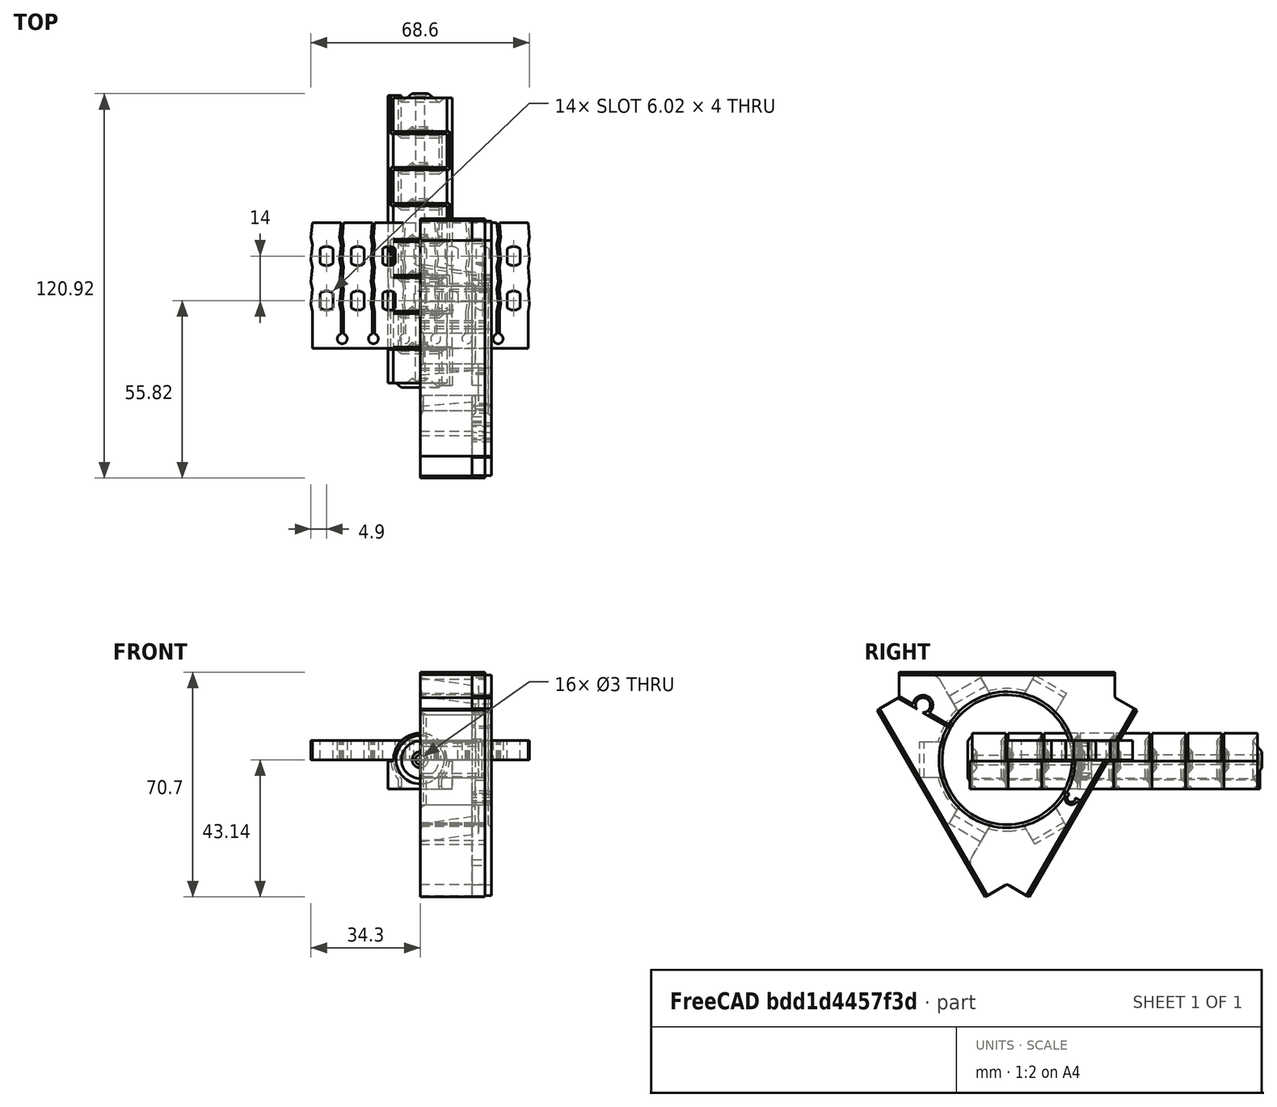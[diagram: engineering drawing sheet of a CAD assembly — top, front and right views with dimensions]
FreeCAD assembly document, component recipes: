
FREECAD ASSEMBLY — COMPONENT RECIPES ("BaseHingeModel_ver1.3_BandOnAxis")

This assembly document has 8 components, labeled P0..P7 below (a component is one placed body or linked part). 7 of them carry a construction recipe — the FreeCAD feature program that regenerates the part from scratch, quoted from this document or its linked companion documents; the rest are supplied as boundary geometry only. No exploded tour is included for this assembly.
COMPONENT P0 — geometry summary ("Assembly"; no construction recipe available for this part):
  bounding box: 182.8 x 158.8 x 20.4 mm
  tessellated surface: 20,696 triangles
  volume: 9578097130411803656351970426578674498653964242418576373807381627235447409514995756881183408189511817567906541525464308833607482709359269325981809199022080 mm^3 (1616738801575943140395693637715189882977871249383409942478852649766611869419882643060896964713126329768861879254438412431142423713072396559864123359232% of its bounding box)
COMPONENT P1 — recipe-attached ("BaseHingePart", modeled in this document).
Construction recipe (the document's own serialized feature program — sketch geometry with constraints, then the solid features built on it; lengths are millimeters unless a unit is written):

FEATURE [Sketcher::SketchObject] Sketch007  label="RightCylinderScatch"
  FullyConstrained = true
  MapMode = 5
  Support = -> [XY_Plane002]
  expr: Constraints[10] = Spreadsheet.mmDiskHight
  expr: Constraints[11] = Spreadsheet.mmLedgeStep
  expr: Constraints[12] = Spreadsheet.mmLedgeStep * 2
  expr: Constraints[13] = Spreadsheet.mmLedgeStep
  expr: Constraints[14] = Spreadsheet.mmLedgeStep / 2
  expr: Constraints[16] = Spreadsheet.mmDiskLedge
  expr: Constraints[20] = Spreadsheet.mmDiskLedge * 2
  expr: Constraints[21] = Spreadsheet.mmDiskLedge
  expr: Constraints[34] = Spreadsheet.mmAirSpace / 2
  expr: Constraints[35] = Spreadsheet.mmLedgeStep / 2
  sketch-geometry (12):
    g0: LineSegment StartX=0 StartY=10.9 StartZ=0 EndX=0.84 EndY=10.9 EndZ=0
    g1: LineSegment StartX=0.84 StartY=10.9 StartZ=0 EndX=2.52 EndY=12.3 EndZ=0
    g2: LineSegment StartX=2.52 StartY=12.3 StartZ=0 EndX=5.88 EndY=9.5 EndZ=0
    g3: LineSegment StartX=5.88 StartY=9.5 StartZ=0 EndX=7.56 EndY=10.9 EndZ=0
    g4: LineSegment StartX=7.56 StartY=10.9 StartZ=0 EndX=8.4 EndY=10.9 EndZ=0
    g5: LineSegment StartX=5.88 StartY=-1 StartZ=0 EndX=2.52 EndY=1.8 EndZ=0
    g6: LineSegment StartX=2.52 StartY=1.8 StartZ=0 EndX=0.84 EndY=0.4 EndZ=0
    g7: LineSegment StartX=0.84 StartY=0.4 StartZ=0 EndX=0 EndY=0.4 EndZ=0
    g8: LineSegment StartX=0 StartY=0.4 StartZ=0 EndX=0 EndY=10.9 EndZ=0
    g9: LineSegment StartX=8.4 StartY=0.4 StartZ=0 EndX=7.56 EndY=0.4 EndZ=0
    g10: LineSegment StartX=7.56 StartY=0.4 StartZ=0 EndX=5.88 EndY=-1 EndZ=0
    g11: LineSegment StartX=8.4 StartY=10.9 StartZ=0 EndX=8.4 EndY=0.4 EndZ=0
  constraints (38):
    c: PointOnObject(g0,g-2)
    c: Horizontal(g0)
    c: Coincident(g0,g1)
    c: Coincident(g1,g2)
    c: Coincident(g2,g3)
    c: Coincident(g3,g4)
    c: Horizontal(g4)
    c: Coincident(g5,g6)
    c: Horizontal(g7)
    c: Coincident(g7,g8)
    c: DistanceY(g7,g0) = 10.5
    c: DistanceX(g0,g1) = 1.68
    c: DistanceX(g1,g2) = 3.36
    c: DistanceX(g2,g3) = 1.68
    c: DistanceX(g3,g4) = 0.84
    c: Coincident(g6,g7)
    c: DistanceY(g0,g1) = 1.4
    c: Equal(g0,g7)
    c: Equal(g1,g6)
    c: Coincident(g0,g8)
    c: DistanceY(g2,g1) = 2.8
    c: DistanceY(g2,g3) = 1.4
    c: Parallel(g2,g5)
    c: Coincident(g9,g10)
    c: Coincident(g10,g5)
    c: Parallel(g3,g10)
    c: Equal(g4,g9)
    c: Horizontal(g9)
    c: Vertical(g2,g5)
    c: Parallel(g1,g6)
    c: Vertical(g8)
    c: Coincident(g11,g4)
    c: Coincident(g11,g9)
    c: Vertical(g11)
    c: DistanceY(g-1,g7) = 0.4
    c: DistanceX(g-1,g0) = 0.84
    c: DistanceX(g-1,g0) = 0
    c: Vertical(g1,g5)
FEATURE [Sketcher::SketchObject] Sketch011  label="LeftCylinderScatch"
  FullyConstrained = true
  MapMode = 5
  Support = -> [XY_Plane]
  expr: Constraints[10] = Spreadsheet.mmLedgeStep
  expr: Constraints[11] = Spreadsheet.mmLedgeStep * 2
  expr: Constraints[12] = Spreadsheet.mmLedgeStep
  expr: Constraints[13] = Spreadsheet.mmLedgeStep / 2
  expr: Constraints[15] = Spreadsheet.mmDiskLedge
  expr: Constraints[19] = Spreadsheet.mmDiskLedge * 2
  expr: Constraints[20] = Spreadsheet.mmDiskLedge
  expr: Constraints[33] = Spreadsheet.mmAirSpace / 2
  expr: Constraints[34] = Spreadsheet.mmLedgeStep / 2
  expr: Constraints[9] = Spreadsheet.mmDiskHight
  sketch-geometry (12):
    g0: LineSegment StartX=0 StartY=-0.4 StartZ=0 EndX=0.84 EndY=-0.4 EndZ=0
    g1: LineSegment StartX=0.84 StartY=-0.4 StartZ=0 EndX=2.52 EndY=1 EndZ=0
    g2: LineSegment StartX=2.52 StartY=1 StartZ=0 EndX=5.88 EndY=-1.8 EndZ=0
    g3: LineSegment StartX=5.88 StartY=-1.8 StartZ=0 EndX=7.56 EndY=-0.4 EndZ=0
    g4: LineSegment StartX=7.56 StartY=-0.4 StartZ=0 EndX=8.4 EndY=-0.4 EndZ=0
    g5: LineSegment StartX=5.88 StartY=-12.3 StartZ=0 EndX=2.52 EndY=-9.5 EndZ=0
    g6: LineSegment StartX=2.52 StartY=-9.5 StartZ=0 EndX=0.84 EndY=-10.9 EndZ=0
    g7: LineSegment StartX=0.84 StartY=-10.9 StartZ=0 EndX=0 EndY=-10.9 EndZ=0
    g8: LineSegment StartX=0 StartY=-10.9 StartZ=0 EndX=0 EndY=-0.4 EndZ=0
    g9: LineSegment StartX=8.4 StartY=-10.9 StartZ=0 EndX=7.56 EndY=-10.9 EndZ=0
    g10: LineSegment StartX=7.56 StartY=-10.9 StartZ=0 EndX=5.88 EndY=-12.3 EndZ=0
    g11: LineSegment StartX=8.4 StartY=-0.4 StartZ=0 EndX=8.4 EndY=-10.9 EndZ=0
  constraints (36):
    c: Horizontal(g0)
    c: Coincident(g0,g1)
    c: Coincident(g1,g2)
    c: Coincident(g2,g3)
    c: Coincident(g3,g4)
    c: Horizontal(g4)
    c: Coincident(g5,g6)
    c: Horizontal(g7)
    c: Coincident(g7,g8)
    c: DistanceY(g7,g0) = 10.5
    c: DistanceX(g0,g1) = 1.68
    c: DistanceX(g1,g2) = 3.36
    c: DistanceX(g2,g3) = 1.68
    c: DistanceX(g3,g4) = 0.84
    c: Coincident(g6,g7)
    c: DistanceY(g0,g1) = 1.4
    c: Equal(g0,g7)
    c: Equal(g1,g6)
    c: Coincident(g0,g8)
    c: DistanceY(g2,g1) = 2.8
    c: DistanceY(g2,g3) = 1.4
    c: Parallel(g2,g5)
    c: Coincident(g9,g10)
    c: Coincident(g10,g5)
    c: Parallel(g3,g10)
    c: Equal(g4,g9)
    c: Horizontal(g9)
    c: Vertical(g2,g5)
    c: Parallel(g1,g6)
    c: Vertical(g8)
    c: Coincident(g11,g4)
    c: Coincident(g11,g9)
    c: Vertical(g11)
    c: DistanceY(g0,g-1) = 0.4
    c: DistanceX(g-1,g0) = 0.84
    c: DistanceX(g-1,g0) = 0
FEATURE [PartDesign::Revolution] Revolution  label="RightCylinderRevolution"
  Angle = 360
  Axis = (0,1,0)
  Base = (0,0,0)
  Profile = -> Sketch007
  ReferenceAxis = -> Sketch007 [V_Axis]
  Reversed = true
FEATURE [PartDesign::Revolution] Revolution004  label="LeftCylinderRevolution"
  Angle = 360
  Axis = (0,1,0)
  Base = (0,0,0)
  Profile = -> Sketch011
  ReferenceAxis = -> Sketch011 [V_Axis]
  Reversed = true
FEATURE [Sketcher::SketchObject] Sketch013  label="RightCylinderAxisHoleScatch"
  AttachmentOffset = pos=(0,0,1) rot=(0,0,1;0rad)
  FullyConstrained = true
  MapMode = 5
  Placement = pos=(0,-1,-2e-16) rot=(1,0,0;1.5708rad)
  Support = -> [XZ_Plane002]
  expr: .AttachmentOffset.Base.z = Spreadsheet.mmDiskLedge - Spreadsheet.mmAirSpace / 2
  expr: Constraints[1] = Spreadsheet.mmHoleRadius * 2
  sketch-geometry (1):
    g0: Circle CenterX=0 CenterY=0 CenterZ=0 NormalX=0 NormalY=0 NormalZ=1 AngleXU=0 Radius=1.5
  constraints (2):
    c: Coincident(g0,g-1)
    c: Diameter(g0) = 3
FEATURE [PartDesign::Pocket] Pocket001  label="RightCylinderAxisHole"
  BaseFeature = -> Revolution
  Direction = (0,1,2e-16)
  Length = 23.8
  Length2 = 5
  Profile = -> Sketch013
  ReferenceAxis = -> Sketch013 [N_Axis]
  Type = 0
  expr: Length = 2 * Spreadsheet.mmDiskHight + 2 * Spreadsheet.mmDiskLedge
FEATURE [Sketcher::SketchObject] Sketch014  label="LeftCylinderAxisHoleScatch"
  AttachmentOffset = pos=(0,0,-1) rot=(0,0,1;0rad)
  FullyConstrained = true
  MapMode = 5
  Placement = pos=(0,1,2e-16) rot=(1,0,0;1.5708rad)
  Support = -> [XZ_Plane]
  expr: .AttachmentOffset.Base.z = -(Spreadsheet.mmDiskLedge - Spreadsheet.mmAirSpace / 2)
  expr: Constraints[1] = Spreadsheet.mmHoleRadius * 2
  sketch-geometry (1):
    g0: Circle CenterX=0 CenterY=0 CenterZ=0 NormalX=0 NormalY=0 NormalZ=1 AngleXU=0 Radius=1.5
  constraints (2):
    c: Coincident(g0,g-1)
    c: Diameter(g0) = 3
FEATURE [PartDesign::Pocket] Pocket002  label="LeftCylinderAxisHole"
  BaseFeature = -> Revolution004
  Direction = (0,1,2e-16)
  Length = 21
  Length2 = 5
  Profile = -> Sketch014
  ReferenceAxis = -> Sketch014 [N_Axis]
  Reversed = true
  Type = 0
  expr: Length = Spreadsheet.mmDiskHight * 2
FEATURE [Sketcher::SketchObject] Sketch023  label="RightCylinderConnectedWingScatch"
  AttachmentOffset = pos=(0,0,-0.4) rot=(0,0,1;0rad)
  FullyConstrained = false
  MapMode = 5
  Placement = pos=(0,0.4,1e-16) rot=(1,0,0;1.5708rad)
  Support = -> [XZ_Plane002]
  expr: .AttachmentOffset.Base.z = -Spreadsheet.mmAirSpace / 2
  expr: Constraints[11] = Spreadsheet.mmHingeRadius + Spreadsheet.mmAirSpace
  expr: Constraints[17] = Spreadsheet.mmHingeRadius + Spreadsheet.mmAirSpace
  expr: Constraints[4] = Spreadsheet.mmHingeRadius * 2
  expr: Constraints[7] = Spreadsheet.mmHingeRadius / 5
  expr: Constraints[8] = Spreadsheet.mmAirSpace / 2
  sketch-geometry (9):
    g0: LineSegment StartX=-5.9397 StartY=-9.2 StartZ=0 EndX=10.0705 EndY=-9.2 EndZ=0
    g1: LineSegment StartX=10.0705 StartY=-9.2 StartZ=0 EndX=10.0705 EndY=-0.4 EndZ=0
    g2: LineSegment StartX=10.0705 StartY=-0.4 StartZ=0 EndX=8.39047 EndY=-0.4 EndZ=0
    g3: ArcOfCircle CenterX=0 CenterY=9e-16 CenterZ=0 NormalX=0 NormalY=0 NormalZ=1 AngleXU=0 Radius=8.4 StartAngle=3.92699 EndAngle=6.23555
    g4: LineSegment StartX=-10.8949 StartY=25.2528 StartZ=0 EndX=-10.8949 EndY=-29.472 EndZ=0
    g5: LineSegment StartX=0 StartY=0 StartZ=0 EndX=8.39047 EndY=-0.4 EndZ=0
    g6: LineSegment StartX=-5.9397 StartY=-5.9397 StartZ=0 EndX=-5.9397 EndY=-9.2 EndZ=0
    g7: LineSegment StartX=0 StartY=9e-16 StartZ=0 EndX=-20.2547 EndY=-20.2547 EndZ=0
    g8: LineSegment StartX=-5.9397 StartY=-5.9397 StartZ=0 EndX=-5.9397 EndY=-9.42884 EndZ=0
  constraints (24):
    c: Coincident(g0,g1)
    c: Vertical(g1)
    c: Horizontal(g2)
    c: Vertical(g4)
    c: Diameter(g3) = 16.8
    c: Coincident(g2,g1)
    c: Coincident(g5,g2)
    c: DistanceX(g2,g2) = 1.68
    c: DistanceY(g1,g-1) = 0.4
    c: Coincident(g3,g6)
    c: Coincident(g3,g2)
    c: DistanceY(g0,g3) = 9.2
    c: PointOnObject(g3,g7)
    c: Coincident(g7,g3)
    c: Angle(g-2,g7) = 2.35619
    c: PointOnObject(g3,g-2)
    c: Horizontal(g0)
    c: DistanceY(g0,g-1) = 9.2
    c: Vertical(g8)
    c: PointOnObject(g8,g7)
    c: PointOnObject(g8,g3)
    c: PointOnObject(g6,g8)
    c: PointOnObject(g0,g8)
    c: PointOnObject(g6,g0)
FEATURE [PartDesign::Pad] Pad008  label="RightCylinderConnectedWingBody"
  BaseFeature = -> Pocket001
  Direction = (0,-1,-2e-16)
  Length = 10.5
  Length2 = 10
  Profile = -> Sketch023
  ReferenceAxis = -> Sketch023 [N_Axis]
  Reversed = true
  Type = 0
  expr: Length = Spreadsheet.mmDiskHight
FEATURE [Sketcher::SketchObject] Sketch024  label="RightCylinderDisconnectedWingScatch"
  AttachmentOffset = pos=(0,0,0.4) rot=(0,0,1;0rad)
  FullyConstrained = false
  MapMode = 5
  Placement = pos=(0,-0.4,-1e-16) rot=(1,0,0;1.5708rad)
  Support = -> [XZ_Plane002]
  expr: .AttachmentOffset.Base.z = Spreadsheet.mmAirSpace / 2
  expr: Constraints[10] = Spreadsheet.mmHingeRadius * 6 / 5
  expr: Constraints[14] = (Spreadsheet.mmHingeRadius + Spreadsheet.mmAirSpace) * 2
  expr: Constraints[18] = Spreadsheet.mmAirSpace
  expr: Constraints[26] = Spreadsheet.mmAirSpace
  expr: Constraints[29] = Spreadsheet.mmHingeRadius * 2
  expr: Constraints[2] = (Spreadsheet.mmHingeRadius + Spreadsheet.mmAirSpace) * 2
  expr: Constraints[8] = Spreadsheet.mmHingeRadius + Spreadsheet.mmAirSpace
  expr: Constraints[9] = Spreadsheet.mmAirSpace / 2
  sketch-geometry (12):
    g0: Circle CenterX=0 CenterY=0 CenterZ=0 NormalX=0 NormalY=0 NormalZ=1 AngleXU=0 Radius=9.2
    g1: LineSegment StartX=-5.9397 StartY=-5.9397 StartZ=0 EndX=-5.9397 EndY=-9.59435 EndZ=0
    g2: LineSegment StartX=-10.08 StartY=-0.4 StartZ=0 EndX=-10.08 EndY=-9.2 EndZ=0
    g3: LineSegment StartX=-10.08 StartY=-9.2 StartZ=0 EndX=-5.9397 EndY=-9.2 EndZ=0
    g4: LineSegment StartX=-6.7397 StartY=-8.4 StartZ=0 EndX=-6.7397 EndY=-6.26231 EndZ=0
    g5: LineSegment StartX=-9.1913 StartY=-0.4 StartZ=0 EndX=-10.08 EndY=-0.4 EndZ=0
    g6: LineSegment StartX=0 StartY=0 StartZ=0 EndX=-7.18968 EndY=-7.18968 EndZ=0
    g7: ArcOfCircle CenterX=0 CenterY=0 CenterZ=0 NormalX=0 NormalY=0 NormalZ=1 AngleXU=0 Radius=9.2 StartAngle=3.18508 EndAngle=3.89029
    g8: LineSegment StartX=-6.7397 StartY=-9.55843 StartZ=0 EndX=-6.7397 EndY=-4.9559 EndZ=0
    g9: LineSegment StartX=-6.7397 StartY=-8.4 StartZ=0 EndX=-5.9397 EndY=-8.4 EndZ=0
    g10: LineSegment StartX=-5.9397 StartY=-8.4 StartZ=0 EndX=-5.9397 EndY=-9.2 EndZ=0
    g11: Circle CenterX=0 CenterY=0 CenterZ=0 NormalX=0 NormalY=0 NormalZ=1 AngleXU=0 Radius=8.4
  constraints (33):
    c: Coincident(g0,g-1)
    c: Vertical(g1)
    c: Diameter(g0) = 18.4
    c: Vertical(g2)
    c: Coincident(g2,g3)
    c: Horizontal(g3)
    c: Coincident(g5,g2)
    c: Horizontal(g5)
    c: DistanceY(g2,g-1) = 9.2
    c: DistanceY(g2,g-1) = 0.4
    c: DistanceX(g2,g0) = 10.08
    c: Coincident(g6,g0)
    c: Angle(g-2,g6) = 2.35619
    c: Coincident(g7,g0)
    c: Diameter(g7) = 18.4
    c: Coincident(g7,g4)
    c: Coincident(g7,g5)
    c: Vertical(g8)
    c: DistanceX(g8,g1) = 0.8
    c: Coincident(g4,g9)
    c: PointOnObject(g9,g1)
    c: Horizontal(g9)
    c: Coincident(g9,g10)
    c: PointOnObject(g10,g1)
    c: PointOnObject(g3,g1)
    c: PointOnObject(g10,g3)
    c: DistanceY(g3,g9) = 0.8
    c: PointOnObject(g4,g8)
    c: Coincident(g11,g7)
    c: Diameter(g11) = 16.8
    c: PointOnObject(g1,g11)
    c: PointOnObject(g1,g6)
    c: PointOnObject(g4,g8)
FEATURE [PartDesign::Pad] Pad009  label="RightCylinderDisconnectedWingBody"
  BaseFeature = -> Pad008
  Direction = (0,-1,-2e-16)
  Length = 12.1
  Length2 = 10
  Profile = -> Sketch024
  ReferenceAxis = -> Sketch024 [N_Axis]
  Reversed = true
  Type = 0
  expr: Length = Spreadsheet.mmDiskHight + Spreadsheet.mmAirSpace * 2
FEATURE [Sketcher::SketchObject] Sketch025  label="LeftCylinderConnectedWingScatch"
  AttachmentOffset = pos=(0,0,0.4) rot=(0,0,1;0rad)
  FullyConstrained = false
  MapMode = 5
  Placement = pos=(0,-0.4,-1e-16) rot=(1,0,0;1.5708rad)
  Support = -> [XZ_Plane]
  expr: .AttachmentOffset.Base.z = Spreadsheet.mmAirSpace / 2
  expr: Constraints[10] = Spreadsheet.mmAirSpace / 2
  expr: Constraints[11] = Spreadsheet.mmHingeRadius + Spreadsheet.mmAirSpace
  expr: Constraints[15] = Spreadsheet.mmHingeRadius * 2
  expr: Constraints[2] = Spreadsheet.mmHingeRadius * 2
  expr: Constraints[9] = Spreadsheet.mmHingeRadius * 6 / 5
  sketch-geometry (8):
    g0: LineSegment StartX=0 StartY=0 StartZ=0 EndX=8.8497 EndY=-8.8497 EndZ=0
    g1: Circle CenterX=0 CenterY=0 CenterZ=0 NormalX=0 NormalY=0 NormalZ=1 AngleXU=0 Radius=8.4
    g2: LineSegment StartX=-10.08 StartY=-0.4 StartZ=0 EndX=-10.08 EndY=-9.2 EndZ=0
    g3: LineSegment StartX=-10.08 StartY=-9.2 StartZ=0 EndX=5.9397 EndY=-9.2 EndZ=0
    g4: LineSegment StartX=5.9397 StartY=-9.2 StartZ=0 EndX=5.9397 EndY=-5.9397 EndZ=0
    g5: LineSegment StartX=-8.39047 StartY=-0.4 StartZ=0 EndX=-10.08 EndY=-0.4 EndZ=0
    g6: ArcOfCircle CenterX=0 CenterY=0 CenterZ=0 NormalX=0 NormalY=0 NormalZ=1 AngleXU=0 Radius=8.4 StartAngle=3.18923 EndAngle=5.49779
    g7: LineSegment StartX=5.9397 StartY=-5.9397 StartZ=0 EndX=5.9397 EndY=-9.58153 EndZ=0
  constraints (24):
    c: Coincident(g0,g-1)
    c: Coincident(g1,g0)
    c: Diameter(g1) = 16.8
    c: Vertical(g2)
    c: Coincident(g2,g3)
    c: Horizontal(g3)
    c: Coincident(g5,g2)
    c: Horizontal(g5)
    c: PointOnObject(g5,g1)
    c: DistanceX(g2,g0) = 10.08
    c: DistanceY(g2,g-1) = 0.4
    c: DistanceY(g2,g-1) = 9.2
    c: Angle(g0,g-2) = 2.35619
    c: PointOnObject(g4,g0)
    c: Coincident(g6,g0)
    c: Diameter(g6) = 16.8
    c: Coincident(g6,g5)
    c: Coincident(g6,g4)
    c: Vertical(g7)
    c: PointOnObject(g7,g1)
    c: PointOnObject(g7,g0)
    c: PointOnObject(g4,g7)
    c: PointOnObject(g3,g7)
    c: PointOnObject(g4,g3)
FEATURE [PartDesign::Pad] Pad010  label="LeftCylinderConnectedWingBody"
  BaseFeature = -> Pocket002
  Direction = (0,-1,-2e-16)
  Length = 10.5
  Length2 = 10
  Profile = -> Sketch025
  ReferenceAxis = -> Sketch025 [N_Axis]
  Type = 0
  expr: Length = Spreadsheet.mmDiskHight
FEATURE [Sketcher::SketchObject] Sketch026  label="LeftCylinderDisconnectedWingScatch"
  AttachmentOffset = pos=(0,0,-0.4) rot=(0,0,1;0rad)
  FullyConstrained = false
  MapMode = 5
  Placement = pos=(0,0.4,1e-16) rot=(1,0,0;1.5708rad)
  Support = -> [XZ_Plane]
  expr: .AttachmentOffset.Base.z = -Spreadsheet.mmAirSpace / 2
  expr: Constraints[10] = Spreadsheet.mmHingeRadius + Spreadsheet.mmAirSpace
  expr: Constraints[16] = Spreadsheet.mmAirSpace
  expr: Constraints[18] = (Spreadsheet.mmHingeRadius + Spreadsheet.mmAirSpace) * 2
  expr: Constraints[26] = Spreadsheet.mmAirSpace
  expr: Constraints[29] = Spreadsheet.mmHingeRadius * 2
  expr: Constraints[2] = (Spreadsheet.mmHingeRadius + Spreadsheet.mmAirSpace) * 2
  expr: Constraints[8] = Spreadsheet.mmAirSpace / 2
  expr: Constraints[9] = Spreadsheet.mmHingeRadius / 5 * 6
  sketch-geometry (12):
    g0: LineSegment StartX=0 StartY=0 StartZ=0 EndX=9.28474 EndY=-9.28474 EndZ=0
    g1: ArcOfCircle CenterX=0 CenterY=0 CenterZ=0 NormalX=0 NormalY=0 NormalZ=1 AngleXU=0 Radius=9.2 StartAngle=5.53449 EndAngle=6.23969
    g2: LineSegment StartX=9.1913 StartY=-0.4 StartZ=0 EndX=10.08 EndY=-0.4 EndZ=0
    g3: LineSegment StartX=10.08 StartY=-0.4 StartZ=0 EndX=10.08 EndY=-9.2 EndZ=0
    g4: LineSegment StartX=10.08 StartY=-9.2 StartZ=0 EndX=5.9397 EndY=-9.2 EndZ=0
    g5: LineSegment StartX=6.7397 StartY=-8.4 StartZ=0 EndX=6.7397 EndY=-6.26231 EndZ=0
    g6: LineSegment StartX=5.9397 StartY=-5.9397 StartZ=0 EndX=5.9397 EndY=-9.17966 EndZ=0
    g7: LineSegment StartX=6.7397 StartY=-5.451 StartZ=0 EndX=6.7397 EndY=-9.15329 EndZ=0
    g8: Circle CenterX=0 CenterY=0 CenterZ=0 NormalX=0 NormalY=0 NormalZ=1 AngleXU=0 Radius=9.2
    g9: LineSegment StartX=6.7397 StartY=-8.4 StartZ=0 EndX=5.9397 EndY=-8.4 EndZ=0
    g10: LineSegment StartX=5.9397 StartY=-8.4 StartZ=0 EndX=5.9397 EndY=-9.2 EndZ=0
    g11: Circle CenterX=0 CenterY=0 CenterZ=0 NormalX=0 NormalY=0 NormalZ=1 AngleXU=0 Radius=8.4
  constraints (33):
    c: Coincident(g0,g-1)
    c: Coincident(g1,g0)
    c: Diameter(g1) = 18.4
    c: Horizontal(g2)
    c: Coincident(g2,g3)
    c: Vertical(g3)
    c: Coincident(g3,g4)
    c: Horizontal(g4)
    c: DistanceY(g2,g-1) = 0.4
    c: DistanceX(g-1,g2) = 10.08
    c: DistanceY(g3,g-1) = 9.2
    c: Angle(g0,g-2) = 2.35619
    c: Coincident(g1,g2)
    c: Coincident(g1,g5)
    c: Vertical(g6)
    c: Vertical(g7)
    c: DistanceX(g6,g7) = 0.8
    c: Coincident(g8,g1)
    c: Diameter(g8) = 18.4
    c: PointOnObject(g5,g7)
    c: Coincident(g5,g9)
    c: PointOnObject(g9,g6)
    c: Horizontal(g9)
    c: Coincident(g9,g10)
    c: PointOnObject(g10,g6)
    c: PointOnObject(g4,g6)
    c: DistanceY(g4,g9) = 0.8
    c: PointOnObject(g10,g4)
    c: Coincident(g11,g1)
    c: Diameter(g11) = 16.8
    c: PointOnObject(g6,g11)
    c: PointOnObject(g6,g0)
    c: PointOnObject(g1,g7)
FEATURE [PartDesign::Pad] Pad011  label="LeftCylinderDisconnectedWingBody"
  BaseFeature = -> Pad010
  Direction = (0,-1,-2e-16)
  Length = 12.1
  Length2 = 10
  Profile = -> Sketch026
  ReferenceAxis = -> Sketch026 [N_Axis]
  Type = 0
  expr: Length = Spreadsheet.mmDiskHight + Spreadsheet.mmAirSpace * 2
FEATURE [Sketcher::SketchObject] Sketch046  label="LeftCylinderSeparatorScatch"
  AttachmentOffset = pos=(0,0,-0.4) rot=(0,0,1;0rad)
  FullyConstrained = false
  MapMode = 5
  Placement = pos=(0,0.4,1e-16) rot=(1,0,0;1.5708rad)
  Support = -> [XZ_Plane]
  expr: .AttachmentOffset.Base.z = -Spreadsheet.mmAirSpace / 2
  expr: Constraints[14] = Spreadsheet.mmAirSpace
  expr: Constraints[15] = Spreadsheet.mmHingeRadius * 2
  expr: Constraints[2] = Spreadsheet.mmHingeRadius + Spreadsheet.mmAirSpace
  expr: Constraints[6] = Spreadsheet.mmAirSpace
  expr: Constraints[7] = (Spreadsheet.mmHingeRadius + Spreadsheet.mmAirSpace) * 2
  sketch-geometry (9):
    g0: LineSegment StartX=0 StartY=0 StartZ=0 EndX=9.28922 EndY=-9.28922 EndZ=0
    g1: LineSegment StartX=6.7397 StartY=-9.2 StartZ=0 EndX=5.9397 EndY=-9.2 EndZ=0
    g2: LineSegment StartX=6.7397 StartY=-8.4 StartZ=0 EndX=6.7397 EndY=-9.2 EndZ=0
    g3: LineSegment StartX=5.9397 StartY=-5.9397 StartZ=0 EndX=5.9397 EndY=-8.88748 EndZ=0
    g4: LineSegment StartX=6.7397 StartY=-5.40605 StartZ=0 EndX=6.7397 EndY=-8.88997 EndZ=0
    g5: Circle CenterX=0 CenterY=0 CenterZ=0 NormalX=0 NormalY=0 NormalZ=1 AngleXU=0 Radius=9.2
    g6: LineSegment StartX=6.7397 StartY=-8.4 StartZ=0 EndX=5.9397 EndY=-8.4 EndZ=0
    g7: LineSegment StartX=5.9397 StartY=-8.4 StartZ=0 EndX=5.9397 EndY=-9.2 EndZ=0
    g8: Circle CenterX=0 CenterY=0 CenterZ=0 NormalX=0 NormalY=0 NormalZ=1 AngleXU=0 Radius=8.4
  constraints (23):
    c: Coincident(g0,g-1)
    c: Horizontal(g1)
    c: DistanceY(g1,g-1) = 9.2
    c: Angle(g0,g-2) = 2.35619
    c: Vertical(g3)
    c: Vertical(g4)
    c: DistanceX(g3,g4) = 0.8
    c: Diameter(g5) = 18.4
    c: PointOnObject(g2,g4)
    c: Coincident(g2,g6)
    c: PointOnObject(g6,g3)
    c: Horizontal(g6)
    c: Coincident(g6,g7)
    c: PointOnObject(g7,g3)
    c: DistanceY(g1,g6) = 0.8
    c: Diameter(g8) = 16.8
    c: PointOnObject(g3,g8)
    c: PointOnObject(g3,g0)
    c: PointOnObject(g1,g4)
    c: Coincident(g2,g1)
    c: Coincident(g0,g8)
    c: Coincident(g0,g5)
    c: Coincident(g7,g1)
FEATURE [PartDesign::Pocket] Pocket004  label="LeftCylinderSeparator"
  BaseFeature = -> Pad011
  Direction = (0,1,2e-16)
  Length = 10.5
  Length2 = 5
  Profile = -> Sketch046
  ReferenceAxis = -> Sketch046 [N_Axis]
  Reversed = true
  Type = 0
  expr: Length = Spreadsheet.mmDiskHight
FEATURE [PartDesign::Body] Body  label="LeftCylinder"
  Group = -> [Sketch011,Revolution004,Sketch014,Pocket002,Sketch025,Pad010,Sketch026,Pad011,Sketch046,Pocket004]
  Origin = -> Origin
  Tip = -> Pocket004
FEATURE [Sketcher::SketchObject] Sketch047  label="RightCylinderSeparatorScatch"
  AttachmentOffset = pos=(0,0,0.4) rot=(0,0,1;0rad)
  FullyConstrained = false
  MapMode = 5
  Placement = pos=(0,-0.4,-1e-16) rot=(1,0,0;1.5708rad)
  Support = -> [XZ_Plane002]
  expr: .AttachmentOffset.Base.z = Spreadsheet.mmAirSpace / 2
  expr: Constraints[15] = Spreadsheet.mmAirSpace
  expr: Constraints[17] = Spreadsheet.mmHingeRadius * 2
  expr: Constraints[2] = (Spreadsheet.mmHingeRadius + Spreadsheet.mmAirSpace) * 2
  expr: Constraints[4] = Spreadsheet.mmHingeRadius + Spreadsheet.mmAirSpace
  expr: Constraints[8] = Spreadsheet.mmAirSpace
  sketch-geometry (9):
    g0: Circle CenterX=0 CenterY=0 CenterZ=0 NormalX=0 NormalY=0 NormalZ=1 AngleXU=0 Radius=9.2
    g1: LineSegment StartX=-5.9397 StartY=-5.9397 StartZ=0 EndX=-5.9397 EndY=-9.59435 EndZ=0
    g2: LineSegment StartX=-6.7397 StartY=-9.2 StartZ=0 EndX=-5.9397 EndY=-9.2 EndZ=0
    g3: LineSegment StartX=0 StartY=0 StartZ=0 EndX=-7.19425 EndY=-7.19425 EndZ=0
    g4: LineSegment StartX=-6.7397 StartY=-9.55843 StartZ=0 EndX=-6.7397 EndY=-4.9559 EndZ=0
    g5: LineSegment StartX=-6.7397 StartY=-8.4 StartZ=0 EndX=-5.9397 EndY=-8.4 EndZ=0
    g6: LineSegment StartX=-5.9397 StartY=-8.4 StartZ=0 EndX=-5.9397 EndY=-9.2 EndZ=0
    g7: Circle CenterX=0 CenterY=0 CenterZ=0 NormalX=0 NormalY=0 NormalZ=1 AngleXU=0 Radius=8.4
    g8: LineSegment StartX=-6.7397 StartY=-8.4 StartZ=0 EndX=-6.7397 EndY=-9.2 EndZ=0
  constraints (24):
    c: Coincident(g0,g-1)
    c: Vertical(g1)
    c: Diameter(g0) = 18.4
    c: Horizontal(g2)
    c: DistanceY(g2,g-1) = 9.2
    c: Coincident(g3,g0)
    c: Angle(g-2,g3) = 2.35619
    c: Vertical(g4)
    c: DistanceX(g4,g1) = 0.8
    c: PointOnObject(g5,g1)
    c: Horizontal(g5)
    c: Coincident(g5,g6)
    c: PointOnObject(g6,g1)
    c: PointOnObject(g2,g1)
    c: PointOnObject(g6,g2)
    c: DistanceY(g2,g5) = 0.8
    c: PointOnObject(g5,g4)
    c: Diameter(g7) = 16.8
    c: PointOnObject(g1,g7)
    c: PointOnObject(g1,g3)
    c: PointOnObject(g2,g4)
    c: Coincident(g8,g5)
    c: Coincident(g8,g2)
    c: Coincident(g0,g7)
FEATURE [PartDesign::Pocket] Pocket005  label="RightCylinderSeparator"
  BaseFeature = -> Pad009
  Direction = (0,1,2e-16)
  Length = 10.5
  Length2 = 5
  Profile = -> Sketch047
  ReferenceAxis = -> Sketch047 [N_Axis]
  Type = 0
  expr: Length = Spreadsheet.mmDiskHight
FEATURE [PartDesign::Body] Body001  label="RightCylinder"
  Group = -> [Sketch007,Revolution,Sketch013,Pocket001,Sketch023,Pad008,Sketch024,Pad009,Sketch047,Pocket005]
  Origin = -> Origin002
  Tip = -> Pocket005
COMPONENT P2 — recipe-attached ("BeamFixatoPart", modeled in this document).
Construction recipe (the document's own serialized feature program — sketch geometry with constraints, then the solid features built on it; lengths are millimeters unless a unit is written):

FEATURE [Sketcher::SketchObject] Sketch022  label="FixatorBodySketch"
  FullyConstrained = false
  MapMode = 5
  Support = -> [XY_Plane005]
  expr: Constraints[143] = Spreadsheet.mmCellWall
  expr: Constraints[144] = Spreadsheet.mmCellWall
  expr: Constraints[145] = Spreadsheet.mmCellWall
  expr: Constraints[146] = Spreadsheet.mmCellWidth
  expr: Constraints[147] = Spreadsheet.mmCellWidth
  expr: Constraints[148] = Spreadsheet.mmCellWidth
  expr: Constraints[169] = Spreadsheet.mmCommonBaseLenght
  expr: Constraints[170] = Spreadsheet.mmToothStep
  expr: Constraints[171] = Spreadsheet.mmToothStep
  expr: Constraints[172] = Spreadsheet.mmToothStep
  expr: Constraints[173] = Spreadsheet.mmToothStep
  expr: Constraints[174] = Spreadsheet.mmToothStep
  expr: Constraints[183] = Spreadsheet.mmCellWall * 3
  expr: Constraints[184] = Spreadsheet.mmCellWall * 3
  expr: Constraints[185] = Spreadsheet.mmCellWall * 3
  expr: Constraints[186] = Spreadsheet.mmCellWall * 3
  expr: Constraints[425] = Spreadsheet.mmFirstCircleArcToBase
  expr: Constraints[435] = Spreadsheet.mmCellWall / 2
  expr: Constraints[464] = Spreadsheet.mmCellWidth + Spreadsheet.mmCellWall
  expr: Constraints[5] = Spreadsheet.mmBaseWidth
  expr: Constraints[6] = Spreadsheet.mmBaseEnd
  sketch-geometry (155):
    g0: LineSegment StartX=-33.9 StartY=0 StartZ=0 EndX=-33.9 EndY=39.5 EndZ=0
    g1: LineSegment StartX=-33.9 StartY=39.5 StartZ=0 EndX=33.9 EndY=39.5 EndZ=0
    g2: LineSegment StartX=33.9 StartY=39.5 StartZ=0 EndX=33.9 EndY=0 EndZ=0
    g3: LineSegment StartX=-73.1099 StartY=25.5 StartZ=0 EndX=65.6354 EndY=25.5 EndZ=0
    g4: LineSegment StartX=-33.9 StartY=0 StartZ=0 EndX=-33.9 EndY=11.5 EndZ=0
    g5: LineSegment StartX=-33.9 StartY=11.5 StartZ=0 EndX=-34.3 EndY=13.9 EndZ=0
    g6: LineSegment StartX=-34.3 StartY=13.9 StartZ=0 EndX=-33.9 EndY=18.5 EndZ=0
    g7: LineSegment StartX=-33.9 StartY=18.5 StartZ=0 EndX=-34.3 EndY=20.9 EndZ=0
    g8: LineSegment StartX=-34.3 StartY=20.9 StartZ=0 EndX=-33.9 EndY=25.5 EndZ=0
    g9: LineSegment StartX=-33.9 StartY=25.5 StartZ=0 EndX=-34.3 EndY=27.9 EndZ=0
    g10: LineSegment StartX=-34.3 StartY=27.9 StartZ=0 EndX=-33.9 EndY=32.5 EndZ=0
    g11: LineSegment StartX=-33.9 StartY=32.5 StartZ=0 EndX=-34.3 EndY=34.9 EndZ=0
    g12: LineSegment StartX=-34.3 StartY=34.9 StartZ=0 EndX=-33.9 EndY=39.5 EndZ=0
    g13: LineSegment StartX=-33.9 StartY=39.5 StartZ=0 EndX=-24.9 EndY=39.5 EndZ=0
    g14: LineSegment StartX=-24.9 StartY=39.5 StartZ=0 EndX=-25.3 EndY=34.9 EndZ=0
    g15: LineSegment StartX=-25.3 StartY=34.9 StartZ=0 EndX=-24.9 EndY=32.5 EndZ=0
    g16: LineSegment StartX=-24.9 StartY=32.5 StartZ=0 EndX=-25.3 EndY=27.9 EndZ=0
    g17: LineSegment StartX=-25.3 StartY=27.9 StartZ=0 EndX=-24.9 EndY=25.5 EndZ=0
    g18: LineSegment StartX=-24.9 StartY=25.5 StartZ=0 EndX=-25.3 EndY=20.9 EndZ=0
    g19: LineSegment StartX=-25.3 StartY=20.9 StartZ=0 EndX=-24.9 EndY=18.5 EndZ=0
    g20: LineSegment StartX=-24.9 StartY=18.5 StartZ=0 EndX=-25.3 EndY=13.9 EndZ=0
    g21: LineSegment StartX=-25.3 StartY=13.9 StartZ=0 EndX=-24.9 EndY=11.5 EndZ=0
    g22: LineSegment StartX=-24.9 StartY=11.5 StartZ=0 EndX=-24.9 EndY=4.5 EndZ=0
    g23: LineSegment StartX=-24.1 StartY=4.5 StartZ=0 EndX=-24.1 EndY=11.5 EndZ=0
    g24: LineSegment StartX=-24.1 StartY=11.5 StartZ=0 EndX=-24.5 EndY=13.9 EndZ=0
    g25: LineSegment StartX=-24.5 StartY=13.9 StartZ=0 EndX=-24.1 EndY=18.5 EndZ=0
    g26: LineSegment StartX=-24.1 StartY=18.5 StartZ=0 EndX=-24.5 EndY=20.9 EndZ=0
    g27: LineSegment StartX=-24.5 StartY=20.9 StartZ=0 EndX=-24.1 EndY=25.5 EndZ=0
    g28: LineSegment StartX=-24.1 StartY=25.5 StartZ=0 EndX=-24.5 EndY=27.9 EndZ=0
    g29: LineSegment StartX=-24.5 StartY=27.9 StartZ=0 EndX=-24.1 EndY=32.5 EndZ=0
    g30: LineSegment StartX=-24.1 StartY=32.5 StartZ=0 EndX=-24.5 EndY=34.9 EndZ=0
    g31: LineSegment StartX=-24.5 StartY=34.9 StartZ=0 EndX=-24.1 EndY=39.5 EndZ=0
    g32: LineSegment StartX=-24.1 StartY=39.5 StartZ=0 EndX=-15.1 EndY=39.5 EndZ=0
    g33: LineSegment StartX=-15.1 StartY=39.5 StartZ=0 EndX=-15.5 EndY=34.9 EndZ=0
    g34: LineSegment StartX=-15.5 StartY=34.9 StartZ=0 EndX=-15.1 EndY=32.5 EndZ=0
    g35: LineSegment StartX=-15.1 StartY=32.5 StartZ=0 EndX=-15.5 EndY=27.9 EndZ=0
    g36: LineSegment StartX=-15.5 StartY=27.9 StartZ=0 EndX=-15.1 EndY=25.5 EndZ=0
    g37: LineSegment StartX=-15.1 StartY=25.5 StartZ=0 EndX=-15.5 EndY=20.9 EndZ=0
    g38: LineSegment StartX=-15.5 StartY=20.9 StartZ=0 EndX=-15.1 EndY=18.5 EndZ=0
    g39: LineSegment StartX=-15.1 StartY=18.5 StartZ=0 EndX=-15.5 EndY=13.9 EndZ=0
    g40: LineSegment StartX=-15.5 StartY=13.9 StartZ=0 EndX=-15.1 EndY=11.5 EndZ=0
    g41: LineSegment StartX=-15.1 StartY=11.5 StartZ=0 EndX=-15.1 EndY=4.5 EndZ=0
    g42: LineSegment StartX=-14.3 StartY=4.5 StartZ=0 EndX=-14.3 EndY=11.5 EndZ=0
    g43: LineSegment StartX=-14.3 StartY=11.5 StartZ=0 EndX=-14.7 EndY=13.9 EndZ=0
    g44: LineSegment StartX=-14.7 StartY=13.9 StartZ=0 EndX=-14.3 EndY=18.5 EndZ=0
    g45: LineSegment StartX=-14.3 StartY=18.5 StartZ=0 EndX=-14.7 EndY=20.9 EndZ=0
    g46: LineSegment StartX=-14.7 StartY=20.9 StartZ=0 EndX=-14.3 EndY=25.5 EndZ=0
    g47: LineSegment StartX=-14.3 StartY=25.5 StartZ=0 EndX=-14.7 EndY=27.9 EndZ=0
    g48: LineSegment StartX=-14.7 StartY=27.9 StartZ=0 EndX=-14.3 EndY=32.5 EndZ=0
    g49: LineSegment StartX=-14.3 StartY=32.5 StartZ=0 EndX=-14.7 EndY=34.9 EndZ=0
    g50: LineSegment StartX=-14.7 StartY=34.9 StartZ=0 EndX=-14.3 EndY=39.5 EndZ=0
    g51: LineSegment StartX=-14.3 StartY=39.5 StartZ=0 EndX=-5.3 EndY=39.5 EndZ=0
    g52: LineSegment StartX=-5.3 StartY=39.5 StartZ=0 EndX=-5.7 EndY=34.9 EndZ=0
    g53: LineSegment StartX=-5.7 StartY=34.9 StartZ=0 EndX=-5.3 EndY=32.5 EndZ=0
    g54: LineSegment StartX=-5.3 StartY=32.5 StartZ=0 EndX=-5.7 EndY=27.9 EndZ=0
    g55: LineSegment StartX=-5.7 StartY=27.9 StartZ=0 EndX=-5.3 EndY=25.5 EndZ=0
    g56: LineSegment StartX=-5.3 StartY=25.5 StartZ=0 EndX=-5.7 EndY=20.9 EndZ=0
    g57: LineSegment StartX=-5.7 StartY=20.9 StartZ=0 EndX=-5.3 EndY=18.5 EndZ=0
    g58: LineSegment StartX=-5.3 StartY=18.5 StartZ=0 EndX=-5.7 EndY=13.9 EndZ=0
    g59: LineSegment StartX=-5.7 StartY=13.9 StartZ=0 EndX=-5.3 EndY=11.5 EndZ=0
    g60: LineSegment StartX=-5.3 StartY=11.5 StartZ=0 EndX=-5.3 EndY=4.5 EndZ=0
    g61: LineSegment StartX=-4.5 StartY=4.5 StartZ=0 EndX=-4.5 EndY=11.5 EndZ=0
    g62: LineSegment StartX=-4.5 StartY=11.5 StartZ=0 EndX=-4.9 EndY=13.9 EndZ=0
    g63: LineSegment StartX=-4.9 StartY=13.9 StartZ=0 EndX=-4.5 EndY=18.5 EndZ=0
    g64: LineSegment StartX=-4.5 StartY=18.5 StartZ=0 EndX=-4.9 EndY=20.9 EndZ=0
    g65: LineSegment StartX=-4.9 StartY=20.9 StartZ=0 EndX=-4.5 EndY=25.5 EndZ=0
    g66: LineSegment StartX=-4.5 StartY=25.5 StartZ=0 EndX=-4.9 EndY=27.9 EndZ=0
    g67: LineSegment StartX=-4.9 StartY=27.9 StartZ=0 EndX=-4.5 EndY=32.5 EndZ=0
    g68: LineSegment StartX=-4.5 StartY=32.5 StartZ=0 EndX=-4.9 EndY=34.9 EndZ=0
    g69: LineSegment StartX=-4.9 StartY=34.9 StartZ=0 EndX=-4.5 EndY=39.5 EndZ=0
    g70: LineSegment StartX=-4.5 StartY=39.5 StartZ=0 EndX=4.5 EndY=39.5 EndZ=0
    g71: LineSegment StartX=4.5 StartY=39.5 StartZ=0 EndX=4.9 EndY=34.9 EndZ=0
    g72: LineSegment StartX=4.9 StartY=34.9 StartZ=0 EndX=4.5 EndY=32.5 EndZ=0
    g73: LineSegment StartX=4.5 StartY=32.5 StartZ=0 EndX=4.9 EndY=27.9 EndZ=0
    g74: LineSegment StartX=4.9 StartY=27.9 StartZ=0 EndX=4.5 EndY=25.5 EndZ=0
    g75: LineSegment StartX=4.5 StartY=25.5 StartZ=0 EndX=4.9 EndY=20.9 EndZ=0
    g76: LineSegment StartX=4.9 StartY=20.9 StartZ=0 EndX=4.5 EndY=18.5 EndZ=0
    g77: LineSegment StartX=4.5 StartY=18.5 StartZ=0 EndX=4.9 EndY=13.9 EndZ=0
    g78: LineSegment StartX=4.9 StartY=13.9 StartZ=0 EndX=4.5 EndY=11.5 EndZ=0
    g79: LineSegment StartX=4.5 StartY=11.5 StartZ=0 EndX=4.5 EndY=4.5 EndZ=0
    g80: LineSegment StartX=5.3 StartY=4.5 StartZ=0 EndX=5.3 EndY=11.5 EndZ=0
    g81: LineSegment StartX=5.3 StartY=11.5 StartZ=0 EndX=5.7 EndY=13.9 EndZ=0
    g82: LineSegment StartX=5.7 StartY=13.9 StartZ=0 EndX=5.3 EndY=18.5 EndZ=0
    g83: LineSegment StartX=5.3 StartY=18.5 StartZ=0 EndX=5.7 EndY=20.9 EndZ=0
    g84: LineSegment StartX=5.7 StartY=20.9 StartZ=0 EndX=5.3 EndY=25.5 EndZ=0
    g85: LineSegment StartX=5.3 StartY=25.5 StartZ=0 EndX=5.7 EndY=27.9 EndZ=0
    g86: LineSegment StartX=5.7 StartY=27.9 StartZ=0 EndX=5.3 EndY=32.5 EndZ=0
    g87: LineSegment StartX=5.3 StartY=32.5 StartZ=0 EndX=5.7 EndY=34.9 EndZ=0
    g88: LineSegment StartX=5.7 StartY=34.9 StartZ=0 EndX=5.3 EndY=39.5 EndZ=0
    g89: LineSegment StartX=5.3 StartY=39.5 StartZ=0 EndX=14.3 EndY=39.5 EndZ=0
    g90: LineSegment StartX=14.3 StartY=39.5 StartZ=0 EndX=14.7 EndY=34.9 EndZ=0
    g91: LineSegment StartX=14.7 StartY=34.9 StartZ=0 EndX=14.3 EndY=32.5 EndZ=0
    g92: LineSegment StartX=14.3 StartY=32.5 StartZ=0 EndX=14.7 EndY=27.9 EndZ=0
    g93: LineSegment StartX=14.7 StartY=27.9 StartZ=0 EndX=14.3 EndY=25.5 EndZ=0
    g94: LineSegment StartX=14.3 StartY=25.5 StartZ=0 EndX=14.7 EndY=20.9 EndZ=0
    g95: LineSegment StartX=14.7 StartY=20.9 StartZ=0 EndX=14.3 EndY=18.5 EndZ=0
    g96: LineSegment StartX=14.3 StartY=18.5 StartZ=0 EndX=14.7 EndY=13.9 EndZ=0
    g97: LineSegment StartX=14.7 StartY=13.9 StartZ=0 EndX=14.3 EndY=11.5 EndZ=0
    g98: LineSegment StartX=14.3 StartY=11.5 StartZ=0 EndX=14.3 EndY=4.5 EndZ=0
    g99: LineSegment StartX=15.1 StartY=4.5 StartZ=0 EndX=15.1 EndY=11.5 EndZ=0
    g100: LineSegment StartX=15.1 StartY=11.5 StartZ=0 EndX=15.5 EndY=13.9 EndZ=0
    g101: LineSegment StartX=15.5 StartY=13.9 StartZ=0 EndX=15.1 EndY=18.5 EndZ=0
    g102: LineSegment StartX=15.1 StartY=18.5 StartZ=0 EndX=15.5 EndY=20.9 EndZ=0
    g103: LineSegment StartX=15.5 StartY=20.9 StartZ=0 EndX=15.1 EndY=25.5 EndZ=0
    g104: LineSegment StartX=15.1 StartY=25.5 StartZ=0 EndX=15.5 EndY=27.9 EndZ=0
    g105: LineSegment StartX=15.5 StartY=27.9 StartZ=0 EndX=15.1 EndY=32.5 EndZ=0
    g106: LineSegment StartX=15.1 StartY=32.5 StartZ=0 EndX=15.5 EndY=34.9 EndZ=0
    g107: LineSegment StartX=15.5 StartY=34.9 StartZ=0 EndX=15.1 EndY=39.5 EndZ=0
    g108: LineSegment StartX=15.1 StartY=39.5 StartZ=0 EndX=24.1 EndY=39.5 EndZ=0
    g109: LineSegment StartX=24.1 StartY=39.5 StartZ=0 EndX=24.5 EndY=34.9 EndZ=0
    g110: LineSegment StartX=24.5 StartY=34.9 StartZ=0 EndX=24.1 EndY=32.5 EndZ=0
    g111: LineSegment StartX=24.1 StartY=32.5 StartZ=0 EndX=24.5 EndY=27.9 EndZ=0
    g112: LineSegment StartX=24.5 StartY=27.9 StartZ=0 EndX=24.1 EndY=25.5 EndZ=0
    g113: LineSegment StartX=24.1 StartY=25.5 StartZ=0 EndX=24.5 EndY=20.9 EndZ=0
    g114: LineSegment StartX=24.5 StartY=20.9 StartZ=0 EndX=24.1 EndY=18.5 EndZ=0
    g115: LineSegment StartX=24.1 StartY=18.5 StartZ=0 EndX=24.5 EndY=13.9 EndZ=0
    g116: LineSegment StartX=24.5 StartY=13.9 StartZ=0 EndX=24.1 EndY=11.5 EndZ=0
    g117: LineSegment StartX=24.1 StartY=11.5 StartZ=0 EndX=24.1 EndY=4.5 EndZ=0
    g118: LineSegment StartX=24.9 StartY=4.5 StartZ=0 EndX=24.9 EndY=11.5 EndZ=0
    g119: LineSegment StartX=24.9 StartY=11.5 StartZ=0 EndX=25.3 EndY=13.9 EndZ=0
    g120: LineSegment StartX=25.3 StartY=13.9 StartZ=0 EndX=24.9 EndY=18.5 EndZ=0
    g121: LineSegment StartX=24.9 StartY=18.5 StartZ=0 EndX=25.3 EndY=20.9 EndZ=0
    g122: LineSegment StartX=25.3 StartY=20.9 StartZ=0 EndX=24.9 EndY=25.5 EndZ=0
    g123: LineSegment StartX=24.9 StartY=25.5 StartZ=0 EndX=25.3 EndY=27.9 EndZ=0
    g124: LineSegment StartX=25.3 StartY=27.9 StartZ=0 EndX=24.9 EndY=32.5 EndZ=0
    g125: LineSegment StartX=24.9 StartY=32.5 StartZ=0 EndX=25.3 EndY=34.9 EndZ=0
    g126: LineSegment StartX=25.3 StartY=34.9 StartZ=0 EndX=24.9 EndY=39.5 EndZ=0
    g127: LineSegment StartX=24.9 StartY=39.5 StartZ=0 EndX=33.9 EndY=39.5 EndZ=0
    g128: LineSegment StartX=33.9 StartY=39.5 StartZ=0 EndX=34.3 EndY=34.9 EndZ=0
    g129: LineSegment StartX=34.3 StartY=34.9 StartZ=0 EndX=33.9 EndY=32.5 EndZ=0
    g130: LineSegment StartX=33.9 StartY=32.5 StartZ=0 EndX=34.3 EndY=27.9 EndZ=0
    g131: LineSegment StartX=34.3 StartY=27.9 StartZ=0 EndX=33.9 EndY=25.5 EndZ=0
    g132: LineSegment StartX=33.9 StartY=25.5 StartZ=0 EndX=34.3 EndY=20.9 EndZ=0
    g133: LineSegment StartX=34.3 StartY=20.9 StartZ=0 EndX=33.9 EndY=18.5 EndZ=0
    g134: LineSegment StartX=33.9 StartY=18.5 StartZ=0 EndX=34.3 EndY=13.9 EndZ=0
    g135: LineSegment StartX=34.3 StartY=13.9 StartZ=0 EndX=33.9 EndY=11.5 EndZ=0
    g136: LineSegment StartX=33.9 StartY=11.5 StartZ=0 EndX=33.9 EndY=0 EndZ=0
    g137: LineSegment StartX=33.9 StartY=0 StartZ=0 EndX=-33.9 EndY=0 EndZ=0
    g138: LineSegment StartX=-73.1099 StartY=18.5 StartZ=0 EndX=65.6354 EndY=18.5 EndZ=0
    g139: LineSegment StartX=-73.1099 StartY=34.9 StartZ=0 EndX=65.6354 EndY=34.9 EndZ=0
    g140: LineSegment StartX=-73.1099 StartY=32.5 StartZ=0 EndX=65.6354 EndY=32.5 EndZ=0
    g141: LineSegment StartX=-73.1099 StartY=27.9 StartZ=0 EndX=65.6354 EndY=27.9 EndZ=0
    g142: LineSegment StartX=-73.1099 StartY=20.9 StartZ=0 EndX=65.6354 EndY=20.9 EndZ=0
    g143: LineSegment StartX=-73.1099 StartY=11.5 StartZ=0 EndX=65.6354 EndY=11.5 EndZ=0
    g144: LineSegment StartX=-34.3 StartY=8.59208 StartZ=0 EndX=-34.3 EndY=49.4346 EndZ=0
    g145: LineSegment StartX=-73.1099 StartY=13.9 StartZ=0 EndX=65.6354 EndY=13.9 EndZ=0
    g146: LineSegment StartX=-33.9 StartY=0 StartZ=0 EndX=33.9 EndY=0 EndZ=0
    g147: LineSegment StartX=-73.1099 StartY=4.5 StartZ=0 EndX=65.6354 EndY=4.5 EndZ=0
    g148: ArcOfCircle CenterX=-24.5 CenterY=3 CenterZ=0 NormalX=0 NormalY=0 NormalZ=1 AngleXU=0 Radius=1.55242 StartAngle=1.8314 EndAngle=7.59338
    g149: ArcOfCircle CenterX=-14.7 CenterY=3 CenterZ=0 NormalX=0 NormalY=0 NormalZ=1 AngleXU=0 Radius=1.55242 StartAngle=1.8314 EndAngle=7.59338
    g150: ArcOfCircle CenterX=-4.9 CenterY=3 CenterZ=0 NormalX=0 NormalY=0 NormalZ=1 AngleXU=0 Radius=1.55242 StartAngle=1.8314 EndAngle=7.59338
    g151: ArcOfCircle CenterX=4.9 CenterY=3 CenterZ=0 NormalX=0 NormalY=0 NormalZ=1 AngleXU=0 Radius=1.55242 StartAngle=1.8314 EndAngle=7.59338
    g152: ArcOfCircle CenterX=14.7 CenterY=3 CenterZ=0 NormalX=0 NormalY=0 NormalZ=1 AngleXU=0 Radius=1.55242 StartAngle=1.8314 EndAngle=7.59338
    g153: ArcOfCircle CenterX=24.5 CenterY=3 CenterZ=0 NormalX=0 NormalY=0 NormalZ=1 AngleXU=0 Radius=1.55242 StartAngle=1.8314 EndAngle=7.59338
    g154: LineSegment StartX=-73.1099 StartY=3 StartZ=0 EndX=65.6354 EndY=3 EndZ=0
  constraints (469):
    c: Coincident(g0,g1)
    c: Coincident(g1,g2)
    c: Horizontal(g3)
    c: Symmetric(g0,g2,g-2)
    c: Symmetric(g1,g0,g-2)
    c: DistanceX(g0,g2) = 67.8
    c: DistanceX(g0,g1) = 67.8
    c: Coincident(g4,g5)
    c: Coincident(g5,g6)
    c: Coincident(g6,g7)
    c: Coincident(g7,g8)
    c: Coincident(g8,g9)
    c: Coincident(g9,g10)
    c: Coincident(g10,g11)
    c: Coincident(g11,g12)
    c: Coincident(g12,g13)
    c: Horizontal(g13)
    c: Coincident(g13,g14)
    c: Coincident(g14,g15)
    c: Coincident(g15,g16)
    c: Coincident(g16,g17)
    c: Coincident(g17,g18)
    c: Coincident(g18,g19)
    c: Coincident(g19,g20)
    c: Coincident(g20,g21)
    c: Coincident(g21,g22)
    c: Coincident(g23,g24)
    c: Coincident(g24,g25)
    c: Coincident(g25,g26)
    c: Coincident(g26,g27)
    c: Coincident(g27,g28)
    c: Coincident(g28,g29)
    c: Coincident(g29,g30)
    c: Coincident(g30,g31)
    c: Coincident(g31,g32)
    c: Horizontal(g32)
    c: Coincident(g32,g33)
    c: Coincident(g33,g34)
    c: Coincident(g34,g35)
    c: Coincident(g35,g36)
    c: Coincident(g36,g37)
    c: Coincident(g37,g38)
    c: Coincident(g38,g39)
    c: Coincident(g39,g40)
    c: Coincident(g40,g41)
    c: Coincident(g42,g43)
    c: Coincident(g43,g44)
    c: Coincident(g44,g45)
    c: Coincident(g45,g46)
    c: Coincident(g46,g47)
    c: Coincident(g47,g48)
    c: Coincident(g48,g49)
    c: Coincident(g49,g50)
    c: Coincident(g50,g51)
    c: Coincident(g51,g52)
    c: Coincident(g52,g53)
    c: Coincident(g53,g54)
    c: Coincident(g54,g55)
    c: Coincident(g55,g56)
    c: Coincident(g56,g57)
    c: Coincident(g57,g58)
    c: Coincident(g58,g59)
    c: Coincident(g59,g60)
    c: Coincident(g61,g62)
    c: Coincident(g62,g63)
    c: Coincident(g63,g64)
    c: Coincident(g64,g65)
    c: Coincident(g65,g66)
    c: Coincident(g66,g67)
    c: Coincident(g67,g68)
    c: Coincident(g68,g69)
    c: Coincident(g69,g70)
    c: Coincident(g70,g71)
    c: Coincident(g71,g72)
    c: Coincident(g72,g73)
    c: Coincident(g73,g74)
    c: Coincident(g74,g75)
    c: Coincident(g75,g76)
    c: Coincident(g76,g77)
    c: Coincident(g77,g78)
    c: Coincident(g78,g79)
    c: Coincident(g80,g81)
    c: Coincident(g81,g82)
    c: Coincident(g82,g83)
    c: Coincident(g83,g84)
    c: Coincident(g84,g85)
    c: Coincident(g85,g86)
    c: Coincident(g86,g87)
    c: Coincident(g87,g88)
    c: Coincident(g88,g89)
    c: Horizontal(g89)
    c: Coincident(g89,g90)
    c: Coincident(g90,g91)
    c: Coincident(g91,g92)
    c: Coincident(g92,g93)
    c: Coincident(g93,g94)
    c: Coincident(g94,g95)
    c: Coincident(g95,g96)
    c: Coincident(g96,g97)
    c: Coincident(g97,g98)
    c: Coincident(g99,g100)
    c: Coincident(g100,g101)
    c: Coincident(g101,g102)
    c: Coincident(g102,g103)
    c: Coincident(g103,g104)
    c: Coincident(g104,g105)
    c: Coincident(g105,g106)
    c: Coincident(g106,g107)
    c: Coincident(g107,g108)
    c: Coincident(g108,g109)
    c: Coincident(g109,g110)
    c: Coincident(g110,g111)
    c: Coincident(g111,g112)
    c: Coincident(g112,g113)
    c: Coincident(g113,g114)
    c: Coincident(g114,g115)
    c: Coincident(g115,g116)
    c: Coincident(g116,g117)
    c: Coincident(g118,g119)
    c: Coincident(g119,g120)
    c: Coincident(g120,g121)
    c: Coincident(g121,g122)
    c: Coincident(g122,g123)
    c: Coincident(g123,g124)
    c: Coincident(g124,g125)
    c: Coincident(g125,g126)
    c: Coincident(g126,g127)
    c: Coincident(g127,g128)
    c: Coincident(g128,g129)
    c: Coincident(g129,g130)
    c: Coincident(g130,g131)
    c: Coincident(g131,g132)
    c: Coincident(g132,g133)
    c: Coincident(g133,g134)
    c: Coincident(g134,g135)
    c: Coincident(g135,g136)
    c: Symmetric(g69,g70,g-2)
    c: Symmetric(g51,g88,g-2)
    c: Symmetric(g50,g89,g-2)
    c: Symmetric(g32,g107,g-2)
    c: Symmetric(g31,g108,g-2)
    c: Symmetric(g13,g126,g-2)
    c: Symmetric(g12,g127,g-2)
    c: DistanceX(g13,g31) = 0.8
    c: DistanceX(g32,g50) = 0.8
    c: DistanceX(g51,g69) = 0.8
    c: DistanceX(g13,g13) = 9
    c: DistanceX(g32,g32) = 9
    c: DistanceX(g51,g51) = 9
    c: Horizontal(g139)
    c: Horizontal(g140)
    c: Horizontal(g141)
    c: Horizontal(g142)
    c: Horizontal(g143)
    c: Vertical(g8,g6)
    c: Vertical(g6,g4)
    c: Vertical(g144)
    c: Horizontal(g145)
    c: Coincident(g146,g0)
    c: Coincident(g146,g2)
    c: Coincident(g0,g137)
    c: Coincident(g2,g137)
    c: Horizontal(g147)
    c: PointOnObject(g11,g139)
    c: PointOnObject(g11,g144)
    c: PointOnObject(g10,g140)
    c: PointOnObject(g9,g144)
    c: PointOnObject(g7,g142)
    c: Horizontal(g138)
    c: DistanceY(g137,g147) = 4.5
    c: DistanceY(g147,g143) = 7
    c: DistanceY(g143,g138) = 7
    c: DistanceY(g138,g3) = 7
    c: DistanceY(g3,g140) = 7
    c: DistanceY(g140,g0) = 7
    c: Vertical(g139,g140)
    c: Vertical(g140,g141)
    c: Vertical(g141,g3)
    c: Vertical(g3,g142)
    c: Vertical(g142,g138)
    c: Vertical(g138,g145)
    c: Vertical(g145,g143)
    c: Vertical(g143,g147)
    c: DistanceY(g143,g145) = 2.4
    c: DistanceY(g138,g142) = 2.4
    c: DistanceY(g3,g141) = 2.4
    c: DistanceY(g140,g139) = 2.4
    c: Parallel(g12,g14)
    c: Parallel(g11,g15)
    c: PointOnObject(g14,g139)
    c: PointOnObject(g30,g139)
    c: PointOnObject(g15,g140)
    c: PointOnObject(g29,g140)
    c: Parallel(g14,g31)
    c: PointOnObject(g16,g141)
    c: PointOnObject(g28,g141)
    c: PointOnObject(g17,g3)
    c: PointOnObject(g27,g3)
    c: PointOnObject(g18,g142)
    c: PointOnObject(g26,g142)
    c: PointOnObject(g19,g138)
    c: PointOnObject(g25,g138)
    c: PointOnObject(g20,g145)
    c: PointOnObject(g24,g145)
    c: PointOnObject(g21,g143)
    c: PointOnObject(g23,g143)
    c: PointOnObject(g22,g147)
    c: PointOnObject(g23,g147)
    c: PointOnObject(g33,g139)
    c: PointOnObject(g49,g139)
    c: PointOnObject(g52,g139)
    c: PointOnObject(g71,g139)
    c: PointOnObject(g87,g139)
    c: PointOnObject(g90,g139)
    c: PointOnObject(g106,g139)
    c: PointOnObject(g109,g139)
    c: PointOnObject(g125,g139)
    c: PointOnObject(g128,g139)
    c: PointOnObject(g34,g140)
    c: PointOnObject(g48,g140)
    c: PointOnObject(g53,g140)
    c: PointOnObject(g67,g140)
    c: PointOnObject(g72,g140)
    c: PointOnObject(g86,g140)
    c: PointOnObject(g91,g140)
    c: PointOnObject(g105,g140)
    c: PointOnObject(g110,g140)
    c: PointOnObject(g124,g140)
    c: PointOnObject(g129,g140)
    c: Parallel(g33,g50)
    c: Parallel(g52,g69)
    c: Parallel(g71,g88)
    c: Parallel(g71,g90)
    c: Parallel(g90,g107)
    c: Parallel(g71,g109)
    c: Parallel(g109,g126)
    c: Parallel(g126,g128)
    c: Symmetric(g71,g68,g-2)
    c: Symmetric(g72,g67,g-2)
    c: Vertical(g139,g140)
    c: Vertical(g140,g141)
    c: Vertical(g141,g3)
    c: Vertical(g3,g142)
    c: Vertical(g142,g138)
    c: Vertical(g138,g145)
    c: Vertical(g145,g143)
    c: Vertical(g143,g147)
    c: Parallel(g34,g49)
    c: Parallel(g49,g53)
    c: Parallel(g53,g68)
    c: Parallel(g35,g48)
    c: Parallel(g48,g54)
    c: Parallel(g54,g67)
    c: PointOnObject(g35,g141)
    c: PointOnObject(g47,g141)
    c: PointOnObject(g54,g141)
    c: PointOnObject(g66,g141)
    c: PointOnObject(g85,g141)
    c: PointOnObject(g92,g141)
    c: PointOnObject(g104,g141)
    c: PointOnObject(g111,g141)
    c: PointOnObject(g123,g141)
    c: PointOnObject(g130,g141)
    c: Symmetric(g66,g73,g-2)
    c: Symmetric(g65,g74,g-2)
    c: PointOnObject(g36,g3)
    c: PointOnObject(g46,g3)
    c: PointOnObject(g55,g3)
    c: PointOnObject(g65,g3)
    c: Parallel(g36,g47)
    c: Parallel(g47,g55)
    c: Parallel(g55,g66)
    c: Symmetric(g64,g75,g-2)
    c: Symmetric(g79,g61,g-2)
    c: Symmetric(g61,g78,g-2)
    c: Symmetric(g62,g77,g-2)
    c: Symmetric(g63,g76,g-2)
    c: Parallel(g37,g46)
    c: Parallel(g46,g56)
    c: Parallel(g56,g65)
    c: PointOnObject(g37,g142)
    c: PointOnObject(g45,g142)
    c: PointOnObject(g56,g142)
    c: PointOnObject(g64,g142)
    c: PointOnObject(g38,g138)
    c: PointOnObject(g44,g138)
    c: PointOnObject(g57,g138)
    c: PointOnObject(g63,g138)
    c: Parallel(g38,g45)
    c: Parallel(g45,g57)
    c: Parallel(g57,g64)
    c: PointOnObject(g39,g145)
    c: PointOnObject(g43,g145)
    c: PointOnObject(g58,g145)
    c: PointOnObject(g62,g145)
    c: Parallel(g39,g44)
    c: Parallel(g44,g58)
    c: Parallel(g58,g63)
    c: Parallel(g40,g43)
    c: Parallel(g43,g59)
    c: Parallel(g59,g62)
    c: PointOnObject(g40,g143)
    c: PointOnObject(g42,g143)
    c: PointOnObject(g59,g143)
    c: PointOnObject(g61,g143)
    c: PointOnObject(g41,g147)
    c: PointOnObject(g42,g147)
    c: PointOnObject(g60,g147)
    c: PointOnObject(g61,g147)
    c: Parallel(g41,g42)
    c: Parallel(g42,g60)
    c: Parallel(g60,g61)
    c: PointOnObject(g80,g147)
    c: PointOnObject(g98,g147)
    c: PointOnObject(g99,g147)
    c: PointOnObject(g117,g147)
    c: PointOnObject(g118,g147)
    c: PointOnObject(g80,g143)
    c: PointOnObject(g97,g143)
    c: PointOnObject(g99,g143)
    c: PointOnObject(g116,g143)
    c: PointOnObject(g118,g143)
    c: PointOnObject(g135,g143)
    c: Parallel(g79,g80)
    c: Parallel(g80,g98)
    c: Parallel(g98,g99)
    c: Parallel(g99,g117)
    c: Parallel(g117,g118)
    c: Parallel(g118,g136)
    c: Parallel(g72,g87)
    c: Parallel(g87,g91)
    c: Parallel(g91,g106)
    c: Parallel(g106,g110)
    c: Parallel(g110,g125)
    c: Parallel(g125,g129)
    c: Parallel(g73,g86)
    c: Parallel(g86,g92)
    c: Parallel(g92,g105)
    c: Parallel(g105,g111)
    c: Parallel(g111,g124)
    c: Parallel(g124,g130)
    c: PointOnObject(g84,g3)
    c: PointOnObject(g93,g3)
    c: PointOnObject(g103,g3)
    c: PointOnObject(g112,g3)
    c: PointOnObject(g122,g3)
    c: PointOnObject(g131,g3)
    c: Parallel(g74,g85)
    c: Parallel(g85,g93)
    c: Parallel(g93,g104)
    c: Parallel(g104,g112)
    c: Parallel(g112,g123)
    c: Parallel(g123,g131)
    c: PointOnObject(g83,g142)
    c: PointOnObject(g94,g142)
    c: PointOnObject(g102,g142)
    c: PointOnObject(g113,g142)
    c: PointOnObject(g121,g142)
    c: PointOnObject(g132,g142)
    c: Parallel(g75,g84)
    c: Parallel(g84,g94)
    c: Parallel(g94,g103)
    c: Parallel(g103,g113)
    c: Parallel(g113,g122)
    c: Parallel(g122,g132)
    c: PointOnObject(g82,g138)
    c: PointOnObject(g95,g138)
    c: PointOnObject(g101,g138)
    c: PointOnObject(g114,g138)
    c: PointOnObject(g120,g138)
    c: PointOnObject(g133,g138)
    c: PointOnObject(g81,g145)
    c: PointOnObject(g96,g145)
    c: PointOnObject(g100,g145)
    c: PointOnObject(g115,g145)
    c: PointOnObject(g119,g145)
    c: PointOnObject(g134,g145)
    c: Parallel(g76,g83)
    c: Parallel(g83,g95)
    c: Parallel(g95,g102)
    c: Parallel(g102,g114)
    c: Parallel(g114,g121)
    c: Parallel(g121,g133)
    c: Parallel(g77,g82)
    c: Parallel(g82,g96)
    c: Parallel(g96,g101)
    c: Parallel(g101,g115)
    c: Parallel(g115,g120)
    c: Parallel(g120,g134)
    c: Parallel(g78,g81)
    c: Parallel(g81,g97)
    c: Parallel(g97,g100)
    c: Parallel(g100,g116)
    c: Parallel(g116,g119)
    c: Parallel(g119,g135)
    c: DistanceY(g137,g-1) = 0
    c: PointOnObject(g148,g154)
    c: PointOnObject(g149,g154)
    c: PointOnObject(g150,g154)
    c: PointOnObject(g151,g154)
    c: PointOnObject(g152,g154)
    c: PointOnObject(g153,g154)
    c: PointOnObject(g22,g148)
    c: PointOnObject(g23,g148)
    c: PointOnObject(g41,g149)
    c: PointOnObject(g42,g149)
    c: PointOnObject(g60,g150)
    c: PointOnObject(g61,g150)
    c: PointOnObject(g79,g151)
    c: PointOnObject(g98,g152)
    c: PointOnObject(g99,g152)
    c: PointOnObject(g117,g153)
    c: PointOnObject(g118,g153)
    c: PointOnObject(g153,g147)
    c: PointOnObject(g153,g147)
    c: PointOnObject(g152,g147)
    c: PointOnObject(g152,g147)
    c: PointOnObject(g151,g147)
    c: PointOnObject(g151,g147)
    c: PointOnObject(g150,g147)
    c: PointOnObject(g150,g147)
    c: PointOnObject(g149,g147)
    c: PointOnObject(g149,g147)
    c: PointOnObject(g148,g147)
    c: PointOnObject(g148,g147)
    c: DistanceY(g154,g147) = 1.5
    c: Vertical(g147,g154)
    c: Vertical(g147,g154)
    c: Coincident(g136,g137)
    c: Coincident(g4,g137)
    c: Coincident(g0,g12)
    c: PointOnObject(g31,g1)
    c: PointOnObject(g50,g1)
    c: PointOnObject(g69,g1)
    c: PointOnObject(g6,g0)
    c: DistanceX(g144,g12) = 0.4
    c: PointOnObject(g9,g141)
    c: PointOnObject(g8,g3)
    c: PointOnObject(g7,g144)
    c: PointOnObject(g6,g138)
    c: PointOnObject(g5,g145)
    c: PointOnObject(g5,g144)
    c: PointOnObject(g4,g143)
    c: Parallel(g12,g33)
    c: Parallel(g12,g52)
    c: Parallel(g15,g30)
    c: Parallel(g11,g34)
    c: PointOnObject(g10,g0)
    c: Parallel(g16,g29)
    c: Parallel(g10,g16)
    c: Parallel(g10,g35)
    c: Parallel(g9,g17)
    c: Parallel(g17,g28)
    c: Parallel(g9,g36)
    c: Parallel(g18,g27)
    c: Parallel(g8,g18)
    c: Parallel(g8,g37)
    c: Parallel(g7,g19)
    c: Parallel(g19,g26)
    c: Parallel(g6,g20)
    c: Parallel(g20,g25)
    c: Parallel(g7,g38)
    c: Parallel(g6,g39)
    c: Symmetric(g150,g151,g-2)
    c: DistanceX(g150,g151) = 9.8
    c: Parallel(g23,g22)
    c: Parallel(g21,g24)
    c: Parallel(g5,g21)
    c: Parallel(g41,g23)
FEATURE [PartDesign::Pad] Pad  label="FixatorPadBody"
  Direction = (0,0,1)
  Length = 6
  Length2 = 10
  Profile = -> Sketch022
  ReferenceAxis = -> Sketch022 [N_Axis]
  Type = 0
  expr: Length = Spreadsheet.mmCellHight
FEATURE [Sketcher::SketchObject] Sketch  label="PiercesPocketSketch"
  AttachmentOffset = pos=(0,0,0) rot=(1,0,0;1.5708rad)
  FullyConstrained = true
  MapMode = 2
  Placement = pos=(0,0,0) rot=(0.707107,0.707107,0;3.14159rad)
  Support = -> [YZ_Plane005]
  expr: Constraints[108] = Spreadsheet.mmCellPierceWidth
  expr: Constraints[118] = Spreadsheet.mmCellPierceWidth
  expr: Constraints[128] = Spreadsheet.mmCellPierceWidth
  expr: Constraints[138] = Spreadsheet.mmCellPierceWidth
  expr: Constraints[148] = Spreadsheet.mmCellPierceWidth
  expr: Constraints[158] = Spreadsheet.mmCellPierceWidth
  expr: Constraints[171] = Spreadsheet.mmCellWidth + Spreadsheet.mmCellWall
  expr: Constraints[172] = Spreadsheet.mmCellWidth + Spreadsheet.mmCellWall
  expr: Constraints[173] = Spreadsheet.mmCellWidth + Spreadsheet.mmCellWall
  expr: Constraints[174] = Spreadsheet.mmCellWidth + Spreadsheet.mmCellWall
  expr: Constraints[175] = Spreadsheet.mmCellWidth + Spreadsheet.mmCellWall
  expr: Constraints[176] = Spreadsheet.mmCellWidth + Spreadsheet.mmCellWall
  expr: Constraints[178] = Spreadsheet.mmCellWidth / 2
  expr: Constraints[179] = Spreadsheet.mmCellWidth / 2
  expr: Constraints[180] = Spreadsheet.mmCommonBaseLenght + Spreadsheet.mmToothStep * 1.5
  expr: Constraints[181] = Spreadsheet.mmToothStep * 2
  expr: Constraints[19] = Spreadsheet.mmCellPierceWidth
  expr: Constraints[29] = Spreadsheet.mmCellPierceWidth
  expr: Constraints[39] = Spreadsheet.mmCellPierceWidth
  expr: Constraints[49] = Spreadsheet.mmCellPierceWidth
  expr: Constraints[59] = Spreadsheet.mmCellPierceWidth
  expr: Constraints[69] = Spreadsheet.mmCellPierceWidth
  expr: Constraints[82] = Spreadsheet.mmCellWidth + Spreadsheet.mmCellWall
  expr: Constraints[83] = Spreadsheet.mmCellWidth + Spreadsheet.mmCellWall
  expr: Constraints[84] = Spreadsheet.mmCellWidth + Spreadsheet.mmCellWall
  expr: Constraints[85] = Spreadsheet.mmCellWidth + Spreadsheet.mmCellWall
  expr: Constraints[86] = Spreadsheet.mmCellWidth + Spreadsheet.mmCellWall
  expr: Constraints[87] = Spreadsheet.mmCellWidth + Spreadsheet.mmCellWall
  expr: Constraints[98] = Spreadsheet.mmCellPierceWidth
  expr: Constraints[9] = Spreadsheet.mmCellPierceWidth
  sketch-geometry (56):
    g0: ArcOfCircle CenterX=29 CenterY=0 CenterZ=0 NormalX=0 NormalY=0 NormalZ=1 AngleXU=0 Radius=3.0104 StartAngle=2.41495 EndAngle=3.86823
    g1: LineSegment StartX=26.75 StartY=2 StartZ=0 EndX=31.25 EndY=2 EndZ=0
    g2: LineSegment StartX=26.75 StartY=-2 StartZ=0 EndX=31.25 EndY=-2 EndZ=0
    g3: ArcOfCircle CenterX=29 CenterY=0 CenterZ=0 NormalX=0 NormalY=0 NormalZ=1 AngleXU=0 Radius=3.0104 StartAngle=5.55654 EndAngle=7.00983
    g4: ArcOfCircle CenterX=29 CenterY=9.8 CenterZ=0 NormalX=0 NormalY=0 NormalZ=1 AngleXU=0 Radius=3.0104 StartAngle=2.41495 EndAngle=3.86823
    g5: LineSegment StartX=26.75 StartY=11.8 StartZ=0 EndX=31.25 EndY=11.8 EndZ=0
    g6: LineSegment StartX=26.75 StartY=7.8 StartZ=0 EndX=31.25 EndY=7.8 EndZ=0
    g7: ArcOfCircle CenterX=29 CenterY=9.8 CenterZ=0 NormalX=0 NormalY=0 NormalZ=1 AngleXU=0 Radius=3.0104 StartAngle=5.55654 EndAngle=7.00983
    g8: ArcOfCircle CenterX=29 CenterY=19.6 CenterZ=0 NormalX=0 NormalY=0 NormalZ=1 AngleXU=0 Radius=3.0104 StartAngle=2.41495 EndAngle=3.86823
    g9: LineSegment StartX=26.75 StartY=21.6 StartZ=0 EndX=31.25 EndY=21.6 EndZ=0
    g10: LineSegment StartX=26.75 StartY=17.6 StartZ=0 EndX=31.25 EndY=17.6 EndZ=0
    g11: ArcOfCircle CenterX=29 CenterY=19.6 CenterZ=0 NormalX=0 NormalY=0 NormalZ=1 AngleXU=0 Radius=3.0104 StartAngle=5.55654 EndAngle=7.00983
    g12: ArcOfCircle CenterX=29 CenterY=29.4 CenterZ=0 NormalX=0 NormalY=0 NormalZ=1 AngleXU=0 Radius=3.0104 StartAngle=2.41495 EndAngle=3.86823
    g13: LineSegment StartX=26.75 StartY=31.4 StartZ=0 EndX=31.25 EndY=31.4 EndZ=0
    g14: LineSegment StartX=26.75 StartY=27.4 StartZ=0 EndX=31.25 EndY=27.4 EndZ=0
    g15: ArcOfCircle CenterX=29 CenterY=29.4 CenterZ=0 NormalX=0 NormalY=0 NormalZ=1 AngleXU=0 Radius=3.0104 StartAngle=5.55654 EndAngle=7.00983
    g16: ArcOfCircle CenterX=29 CenterY=-9.8 CenterZ=0 NormalX=0 NormalY=0 NormalZ=1 AngleXU=0 Radius=3.0104 StartAngle=2.41495 EndAngle=3.86823
    g17: LineSegment StartX=26.75 StartY=-7.8 StartZ=0 EndX=31.25 EndY=-7.8 EndZ=0
    g18: LineSegment StartX=26.75 StartY=-11.8 StartZ=0 EndX=31.25 EndY=-11.8 EndZ=0
    g19: ArcOfCircle CenterX=29 CenterY=-9.8 CenterZ=0 NormalX=0 NormalY=0 NormalZ=1 AngleXU=0 Radius=3.0104 StartAngle=5.55654 EndAngle=7.00983
    g20: ArcOfCircle CenterX=29 CenterY=-19.6 CenterZ=0 NormalX=0 NormalY=0 NormalZ=1 AngleXU=0 Radius=3.0104 StartAngle=2.41495 EndAngle=3.86823
    g21: LineSegment StartX=26.75 StartY=-17.6 StartZ=0 EndX=31.25 EndY=-17.6 EndZ=0
    g22: LineSegment StartX=26.75 StartY=-21.6 StartZ=0 EndX=31.25 EndY=-21.6 EndZ=0
    g23: ArcOfCircle CenterX=29 CenterY=-19.6 CenterZ=0 NormalX=0 NormalY=0 NormalZ=1 AngleXU=0 Radius=3.0104 StartAngle=5.55654 EndAngle=7.00983
    g24: ArcOfCircle CenterX=29 CenterY=-29.4 CenterZ=0 NormalX=0 NormalY=0 NormalZ=1 AngleXU=0 Radius=3.0104 StartAngle=2.41495 EndAngle=3.86823
    g25: LineSegment StartX=26.75 StartY=-27.4 StartZ=0 EndX=31.25 EndY=-27.4 EndZ=0
    g26: LineSegment StartX=26.75 StartY=-31.4 StartZ=0 EndX=31.25 EndY=-31.4 EndZ=0
    g27: ArcOfCircle CenterX=29 CenterY=-29.4 CenterZ=0 NormalX=0 NormalY=0 NormalZ=1 AngleXU=0 Radius=3.0104 StartAngle=5.55654 EndAngle=7.00983
    g28: ArcOfCircle CenterX=15 CenterY=0 CenterZ=0 NormalX=0 NormalY=0 NormalZ=1 AngleXU=0 Radius=3.0104 StartAngle=2.41495 EndAngle=3.86823
    g29: LineSegment StartX=12.75 StartY=2 StartZ=0 EndX=17.25 EndY=2 EndZ=0
    g30: LineSegment StartX=12.75 StartY=-2 StartZ=0 EndX=17.25 EndY=-2 EndZ=0
    g31: ArcOfCircle CenterX=15 CenterY=0 CenterZ=0 NormalX=0 NormalY=0 NormalZ=1 AngleXU=0 Radius=3.0104 StartAngle=5.55654 EndAngle=7.00983
    g32: ArcOfCircle CenterX=15 CenterY=9.8 CenterZ=0 NormalX=0 NormalY=0 NormalZ=1 AngleXU=0 Radius=3.0104 StartAngle=2.41495 EndAngle=3.86823
    g33: LineSegment StartX=12.75 StartY=11.8 StartZ=0 EndX=17.25 EndY=11.8 EndZ=0
    g34: LineSegment StartX=12.75 StartY=7.8 StartZ=0 EndX=17.25 EndY=7.8 EndZ=0
    g35: ArcOfCircle CenterX=15 CenterY=9.8 CenterZ=0 NormalX=0 NormalY=0 NormalZ=1 AngleXU=0 Radius=3.0104 StartAngle=5.55654 EndAngle=7.00983
    g36: ArcOfCircle CenterX=15 CenterY=19.6 CenterZ=0 NormalX=0 NormalY=0 NormalZ=1 AngleXU=0 Radius=3.0104 StartAngle=2.41495 EndAngle=3.86823
    g37: LineSegment StartX=12.75 StartY=21.6 StartZ=0 EndX=17.25 EndY=21.6 EndZ=0
    g38: LineSegment StartX=12.75 StartY=17.6 StartZ=0 EndX=17.25 EndY=17.6 EndZ=0
    g39: ArcOfCircle CenterX=15 CenterY=19.6 CenterZ=0 NormalX=0 NormalY=0 NormalZ=1 AngleXU=0 Radius=3.0104 StartAngle=5.55654 EndAngle=7.00983
    g40: ArcOfCircle CenterX=15 CenterY=29.4 CenterZ=0 NormalX=0 NormalY=0 NormalZ=1 AngleXU=0 Radius=3.0104 StartAngle=2.41495 EndAngle=3.86823
    g41: LineSegment StartX=12.75 StartY=31.4 StartZ=0 EndX=17.25 EndY=31.4 EndZ=0
    g42: LineSegment StartX=12.75 StartY=27.4 StartZ=0 EndX=17.25 EndY=27.4 EndZ=0
    g43: ArcOfCircle CenterX=15 CenterY=29.4 CenterZ=0 NormalX=0 NormalY=0 NormalZ=1 AngleXU=0 Radius=3.0104 StartAngle=5.55654 EndAngle=7.00983
    g44: ArcOfCircle CenterX=15 CenterY=-9.8 CenterZ=0 NormalX=0 NormalY=0 NormalZ=1 AngleXU=0 Radius=3.0104 StartAngle=2.41495 EndAngle=3.86823
    g45: LineSegment StartX=12.75 StartY=-7.8 StartZ=0 EndX=17.25 EndY=-7.8 EndZ=0
    g46: LineSegment StartX=12.75 StartY=-11.8 StartZ=0 EndX=17.25 EndY=-11.8 EndZ=0
    g47: ArcOfCircle CenterX=15 CenterY=-9.8 CenterZ=0 NormalX=0 NormalY=0 NormalZ=1 AngleXU=0 Radius=3.0104 StartAngle=5.55654 EndAngle=7.00983
    g48: ArcOfCircle CenterX=15 CenterY=-19.6 CenterZ=0 NormalX=0 NormalY=0 NormalZ=1 AngleXU=0 Radius=3.0104 StartAngle=2.41495 EndAngle=3.86823
    g49: LineSegment StartX=12.75 StartY=-17.6 StartZ=0 EndX=17.25 EndY=-17.6 EndZ=0
    g50: LineSegment StartX=12.75 StartY=-21.6 StartZ=0 EndX=17.25 EndY=-21.6 EndZ=0
    g51: ArcOfCircle CenterX=15 CenterY=-19.6 CenterZ=0 NormalX=0 NormalY=0 NormalZ=1 AngleXU=0 Radius=3.0104 StartAngle=5.55654 EndAngle=7.00983
    g52: ArcOfCircle CenterX=15 CenterY=-29.4 CenterZ=0 NormalX=0 NormalY=0 NormalZ=1 AngleXU=0 Radius=3.0104 StartAngle=2.41495 EndAngle=3.86823
    g53: LineSegment StartX=12.75 StartY=-27.4 StartZ=0 EndX=17.25 EndY=-27.4 EndZ=0
    g54: LineSegment StartX=12.75 StartY=-31.4 StartZ=0 EndX=17.25 EndY=-31.4 EndZ=0
    g55: ArcOfCircle CenterX=15 CenterY=-29.4 CenterZ=0 NormalX=0 NormalY=0 NormalZ=1 AngleXU=0 Radius=3.0104 StartAngle=5.55654 EndAngle=7.00983
  constraints (182):
    c: Horizontal(g1)
    c: Horizontal(g2)
    c: PointOnObject(g1,g0)
    c: Coincident(g0,g3)
    c: Coincident(g0,g2)
    c: Coincident(g3,g2)
    c: Coincident(g1,g0)
    c: Coincident(g3,g1)
    c: Equal(g2,g1)
    c: DistanceY(g2,g1) = 4
    c: Horizontal(g5)
    c: Horizontal(g6)
    c: PointOnObject(g5,g4)
    c: Coincident(g4,g7)
    c: Coincident(g4,g6)
    c: Coincident(g7,g6)
    c: Coincident(g5,g4)
    c: Coincident(g7,g5)
    c: Equal(g6,g5)
    c: DistanceY(g6,g5) = 4
    c: Horizontal(g9)
    c: Horizontal(g10)
    c: PointOnObject(g9,g8)
    c: Coincident(g8,g11)
    c: Coincident(g8,g10)
    c: Coincident(g11,g10)
    c: Coincident(g9,g8)
    c: Coincident(g11,g9)
    c: Equal(g10,g9)
    c: DistanceY(g10,g9) = 4
    c: Horizontal(g13)
    c: Horizontal(g14)
    c: PointOnObject(g13,g12)
    c: Coincident(g12,g15)
    c: Coincident(g12,g14)
    c: Coincident(g15,g14)
    c: Coincident(g13,g12)
    c: Coincident(g15,g13)
    c: Equal(g14,g13)
    c: DistanceY(g14,g13) = 4
    c: Horizontal(g17)
    c: Horizontal(g18)
    c: PointOnObject(g17,g16)
    c: Coincident(g16,g19)
    c: Coincident(g16,g18)
    c: Coincident(g19,g18)
    c: Coincident(g17,g16)
    c: Coincident(g19,g17)
    c: Equal(g18,g17)
    c: DistanceY(g18,g17) = 4
    c: Horizontal(g21)
    c: Horizontal(g22)
    c: PointOnObject(g21,g20)
    c: Coincident(g20,g23)
    c: Coincident(g20,g22)
    c: Coincident(g23,g22)
    c: Coincident(g21,g20)
    c: Coincident(g23,g21)
    c: Equal(g22,g21)
    c: DistanceY(g22,g21) = 4
    c: Horizontal(g25)
    c: Horizontal(g26)
    c: PointOnObject(g25,g24)
    c: Coincident(g24,g27)
    c: Coincident(g24,g26)
    c: Coincident(g27,g26)
    c: Coincident(g25,g24)
    c: Coincident(g27,g25)
    c: Equal(g26,g25)
    c: DistanceY(g26,g25) = 4
    c: Vertical(g0,g4)
    c: Vertical(g4,g8)
    c: Vertical(g8,g12)
    c: Vertical(g12,g16)
    c: Vertical(g16,g20)
    c: Vertical(g20,g24)
    c: Equal(g2,g18)
    c: Equal(g18,g22)
    c: Equal(g22,g26)
    c: Equal(g1,g5)
    c: Equal(g5,g9)
    c: Equal(g9,g13)
    c: DistanceY(g8,g12) = 9.8
    c: DistanceY(g4,g8) = 9.8
    c: DistanceY(g0,g4) = 9.8
    c: DistanceY(g16,g0) = 9.8
    c: DistanceY(g20,g16) = 9.8
    c: DistanceY(g24,g20) = 9.8
    c: PointOnObject(g0,g-1)
    c: Horizontal(g29)
    c: Horizontal(g30)
    c: PointOnObject(g29,g28)
    c: Coincident(g28,g31)
    c: Coincident(g28,g30)
    c: Coincident(g31,g30)
    c: Coincident(g29,g28)
    c: Coincident(g31,g29)
    c: Equal(g30,g29)
    c: DistanceY(g30,g29) = 4
    c: Horizontal(g33)
    c: Horizontal(g34)
    c: PointOnObject(g33,g32)
    c: Coincident(g32,g35)
    c: Coincident(g32,g34)
    c: Coincident(g35,g34)
    c: Coincident(g33,g32)
    c: Coincident(g35,g33)
    c: Equal(g34,g33)
    c: DistanceY(g34,g33) = 4
    c: Horizontal(g37)
    c: Horizontal(g38)
    c: PointOnObject(g37,g36)
    c: Coincident(g36,g39)
    c: Coincident(g36,g38)
    c: Coincident(g39,g38)
    c: Coincident(g37,g36)
    c: Coincident(g39,g37)
    c: Equal(g38,g37)
    c: DistanceY(g38,g37) = 4
    c: Horizontal(g41)
    c: Horizontal(g42)
    c: PointOnObject(g41,g40)
    c: Coincident(g40,g43)
    c: Coincident(g40,g42)
    c: Coincident(g43,g42)
    c: Coincident(g41,g40)
    c: Coincident(g43,g41)
    c: Equal(g42,g41)
    c: DistanceY(g42,g41) = 4
    c: Horizontal(g45)
    c: Horizontal(g46)
    c: PointOnObject(g45,g44)
    c: Coincident(g44,g47)
    c: Coincident(g44,g46)
    c: Coincident(g47,g46)
    c: Coincident(g45,g44)
    c: Coincident(g47,g45)
    c: Equal(g46,g45)
    c: DistanceY(g46,g45) = 4
    c: Horizontal(g49)
    c: Horizontal(g50)
    c: PointOnObject(g49,g48)
    c: Coincident(g48,g51)
    c: Coincident(g48,g50)
    c: Coincident(g51,g50)
    c: Coincident(g49,g48)
    c: Coincident(g51,g49)
    c: Equal(g50,g49)
    c: DistanceY(g50,g49) = 4
    c: Horizontal(g53)
    c: Horizontal(g54)
    c: PointOnObject(g53,g52)
    c: Coincident(g52,g55)
    c: Coincident(g52,g54)
    c: Coincident(g55,g54)
    c: Coincident(g53,g52)
    c: Coincident(g55,g53)
    c: Equal(g54,g53)
    c: DistanceY(g54,g53) = 4
    c: Vertical(g28,g32)
    c: Vertical(g32,g36)
    c: Vertical(g36,g40)
    c: Vertical(g40,g44)
    c: Vertical(g44,g48)
    c: Vertical(g48,g52)
    c: Equal(g30,g46)
    c: Equal(g46,g50)
    c: Equal(g50,g54)
    c: Equal(g29,g33)
    c: Equal(g33,g37)
    c: Equal(g37,g41)
    c: DistanceY(g36,g40) = 9.8
    c: DistanceY(g32,g36) = 9.8
    c: DistanceY(g28,g32) = 9.8
    c: DistanceY(g44,g28) = 9.8
    c: DistanceY(g48,g44) = 9.8
    c: DistanceY(g52,g48) = 9.8
    c: PointOnObject(g28,g-1)
    c: DistanceX(g24,g26) = 4.5
    c: DistanceX(g52,g54) = 4.5
    c: DistanceX(g-1,g28) = 15
    c: DistanceX(g28,g0) = 14
FEATURE [PartDesign::Pocket] Pocket  label="PiercesPocket"
  BaseFeature = -> Pad
  Direction = (-2e-16,2e-16,1)
  Length = 69.4
  Length2 = 5
  Midplane = true
  Profile = -> Sketch
  ReferenceAxis = -> Sketch [N_Axis]
  Type = 0
  expr: Length = Spreadsheet.mmBaseWidth + Spreadsheet.mmCellWall * 2
FEATURE [PartDesign::Body] Body004  label="BeamFixator"
  Group = -> [Sketch022,Pad,Sketch,Pocket]
  Origin = -> Origin005
  Tip = -> Pocket
COMPONENT P3 — recipe-attached ("HingePart", modeled in this document).
Construction recipe (the document's own serialized feature program — sketch geometry with constraints, then the solid features built on it; lengths are millimeters unless a unit is written):

FEATURE [PartDesign::LinearPattern] LinearPattern
  Direction = -> Sketch007 [V_Axis]
  Length = 67.8
  Occurrences = 4
  Originals = -> [Revolution,Revolution004,Pocket001,Pocket002,Pad008,Pad009,Pad010,Pad011,Pocket004,Pocket005]
  expr: Length = Spreadsheet.mmHingeHight
  expr: Occurrences = Spreadsheet.nHingeHightDiskCnt
FEATURE [PartDesign::Body] Body005
  Group = -> [LinearPattern]
  Origin = -> Origin007
  Tip = -> LinearPattern
COMPONENT P4 — recipe-attached ("AxisFixatorPart", modeled in this document).
Construction recipe (the document's own serialized feature program — sketch geometry with constraints, then the solid features built on it; lengths are millimeters unless a unit is written):

FEATURE [Sketcher::SketchObject] Sketch027  label="CommonFixatorScatch"
  FullyConstrained = false
  MapMode = 5
  Placement = pos=(0,0,0) rot=(0.57735,0.57735,0.57735;2.0944rad)
  Support = -> [YZ_Plane013]
  expr: Constraints[0] = Spreadsheet.mmAxisTubeDia + 2 * Spreadsheet.mmFixatorThick + 2 * Spreadsheet.mmTwoSideTapeThick
  expr: Constraints[17] = Spreadsheet.mmAxisTubeDia / 2 + Spreadsheet.mmPetalHightMax + Spreadsheet.mmTwoSideTapeThick
  expr: Constraints[18] = Spreadsheet.mmAxisTubeDia / 2 + Spreadsheet.mmPetalHightMax + Spreadsheet.mmTwoSideTapeThick
  expr: Constraints[32] = Spreadsheet.mmPetalPocketWidth
  expr: Constraints[33] = Spreadsheet.mmBaseWidth
  expr: Constraints[3] = Spreadsheet.mmAxisTubeDia
  sketch-geometry (14):
    g0: Circle CenterX=0 CenterY=0 CenterZ=0 NormalX=0 NormalY=0 NormalZ=1 AngleXU=0 Radius=26.72
    g1: LineSegment StartX=0 StartY=0 StartZ=0 EndX=32.2586 EndY=18.6245 EndZ=0
    g2: ArcOfCircle CenterX=0 CenterY=0 CenterZ=0 NormalX=0 NormalY=0 NormalZ=1 AngleXU=0 Radius=20.4 StartAngle=5.32461 EndAngle=6.86682
    g3: LineSegment StartX=0 StartY=-20.4 StartZ=0 EndX=0 EndY=-39.1443 EndZ=0
    g4: LineSegment StartX=0 StartY=-39.1443 StartZ=0 EndX=6.1902 EndY=-42.7183 EndZ=0
    g5: LineSegment StartX=6.1902 StartY=-42.7183 StartZ=0 EndX=40.0902 EndY=15.9983 EndZ=0
    g6: LineSegment StartX=40.0902 StartY=15.9983 StartZ=0 EndX=33.9 EndY=19.5722 EndZ=0
    g7: LineSegment StartX=33.9 StartY=19.5722 StartZ=0 EndX=17.6669 EndY=10.2 EndZ=0
    g8: LineSegment StartX=14.7156 StartY=-14.1284 StartZ=0 EndX=17.9224 EndY=-19.6828 EndZ=0
    g9: LineSegment StartX=17.9224 StartY=-19.6828 StartZ=0 EndX=8.08455 EndY=-25.3627 EndZ=0
    g10: LineSegment StartX=8.08455 StartY=-25.3627 StartZ=0 EndX=4.87772 EndY=-19.8083 EndZ=0
    g11: ArcOfCircle CenterX=0 CenterY=0 CenterZ=0 NormalX=0 NormalY=0 NormalZ=1 AngleXU=0 Radius=20.4 StartAngle=4.71239 EndAngle=4.95383
    g12: ArcOfCircle CenterX=0 CenterY=0 CenterZ=0 NormalX=0 NormalY=0 NormalZ=1 AngleXU=0 Radius=20.4 StartAngle=5.51814 EndAngle=6.80678
    g13: LineSegment StartX=0 StartY=0 StartZ=0 EndX=18.7992 EndY=-32.5612 EndZ=0
  constraints (39):
    c: Diameter(g0) = 53.44
    c: Angle(g-1,g1) = 0.523599
    c: PointOnObject(g6,g1)
    c: Diameter(g2) = 40.8
    c: Vertical(g3)
    c: Coincident(g3,g4)
    c: Coincident(g4,g5)
    c: Coincident(g5,g6)
    c: Coincident(g6,g7)
    c: Coincident(g8,g9)
    c: Coincident(g9,g10)
    c: Equal(g2,g11)
    c: Coincident(g2,g11)
    c: PointOnObject(g3,g-2)
    c: Parallel(g4,g6)
    c: Perpendicular(g5,g4)
    c: Tangent(g0,g5)
    c: Distance(g8,g11) = 26.62
    c: Distance(g9,g11) = 26.62
    c: Coincident(g11,g12)
    c: PointOnObject(g7,g1)
    c: Coincident(g10,g11)
    c: Coincident(g11,g3)
    c: Coincident(g12,g8)
    c: PointOnObject(g12,g1)
    c: Coincident(g12,g7)
    c: PointOnObject(g7,g1)
    c: Perpendicular(g10,g9)
    c: Perpendicular(g9,g8)
    c: Coincident(g13,g11)
    c: Angle(g13,g-1) = 1.0472
    c: Symmetric(g10,g8,g13)
    c: Distance(g10,g8) = 11.3598
    c: Distance(g4,g5) = 67.8
    c: Equal(g4,g6)
    c: Equal(g3,g7)
    c: Coincident(g-1,g0)
    c: Coincident(g0,g11)
    c: Coincident(g11,g1)
FEATURE [PartDesign::Pad] Pad012  label="AxisFixatorBodyPad"
  Direction = (1,-2e-16,3e-16)
  Length = 20.4
  Length2 = 10
  Placement = pos=(0,0,0) rot=(0.57735,0.57735,0.57735;2.0944rad)
  Profile = -> Sketch027
  ReferenceAxis = -> Sketch027 [N_Axis]
  Type = 0
  expr: Length = Spreadsheet.mmFixatorHight
FEATURE [Sketcher::SketchObject] Sketch031  label="MaxPetalBase001"
  FullyConstrained = false
  MapMode = 5
  Placement = pos=(0,0,0) rot=(0.57735,0.57735,0.57735;2.0944rad)
  Support = -> [YZ_Plane013]
  expr: Constraints[0] = Spreadsheet.mmAxisTubeDia + 2 * Spreadsheet.mmFixatorThick
  expr: Constraints[10] = Spreadsheet.mmAxisTubeDia
  expr: Constraints[12] = Spreadsheet.mmPetalPocketWidth
  expr: Constraints[1] = Spreadsheet.mmAxisTubeDia
  expr: Constraints[6] = Spreadsheet.mmAxisTubeDia / 2 + Spreadsheet.mmPetalHightMax
  sketch-geometry (7):
    g0: Circle CenterX=0 CenterY=2.5e-15 CenterZ=0 NormalX=0 NormalY=0 NormalZ=1 AngleXU=0 Radius=39.855
    g1: Circle CenterX=0 CenterY=2.5e-15 CenterZ=0 NormalX=0 NormalY=0 NormalZ=1 AngleXU=0 Radius=26.62
    g2: ArcOfCircle CenterX=0 CenterY=2.5e-15 CenterZ=0 NormalX=0 NormalY=0 NormalZ=1 AngleXU=0 Radius=20.4 StartAngle=5.86056 EndAngle=6.76902
    g3: LineSegment StartX=19.5933 StartY=5.67991 StartZ=0 EndX=26.52 EndY=5.67991 EndZ=0
    g4: LineSegment StartX=26.52 StartY=5.67991 StartZ=0 EndX=26.52 EndY=-5.67991 EndZ=0
    g5: LineSegment StartX=26.52 StartY=-5.67991 StartZ=0 EndX=19.5933 EndY=-5.67991 EndZ=0
    g6: ArcOfCircle CenterX=0 CenterY=2.5e-15 CenterZ=0 NormalX=0 NormalY=0 NormalZ=1 AngleXU=0 Radius=20.4 StartAngle=6.00103 EndAngle=6.56534
  constraints (17):
    c: Diameter(g1) = 53.24
    c: Diameter(g2) = 40.8
    c: Coincident(g3,g4)
    c: Coincident(g4,g5)
    c: Coincident(g0,g2)
    c: Vertical(g4)
    c: DistanceX(g-1,g4) = 26.52
    c: Coincident(g6,g0)
    c: Coincident(g6,g3)
    c: Coincident(g6,g5)
    c: Diameter(g6) = 40.8
    c: Symmetric(g3,g5,g-1)
    c: DistanceY(g5,g3) = 11.3598
    c: Horizontal(g3)
    c: Horizontal(g5)
    c: Coincident(g1,g6)
    c: Coincident(g-1,g6)
FEATURE [Sketcher::SketchObject] Sketch032  label="MinPetalBase001"
  AttachmentOffset = pos=(0,0,18.36) rot=(0,0,1;0rad)
  FullyConstrained = false
  MapMode = 5
  Placement = pos=(18.36,-4.1e-15,4.1e-15) rot=(0.57735,0.57735,0.57735;2.0944rad)
  Support = -> [YZ_Plane013]
  expr: .AttachmentOffset.Base.z = Spreadsheet.mmFixatorHight * 0.9
  expr: Constraints[0] = Spreadsheet.mmAxisTubeDia + 2 * Spreadsheet.mmFixatorThick
  expr: Constraints[10] = Spreadsheet.mmAxisTubeDia
  expr: Constraints[12] = Spreadsheet.mmPetalPocketWidth
  expr: Constraints[1] = Spreadsheet.mmAxisTubeDia
  expr: Constraints[6] = Spreadsheet.mmAxisTubeDia / 2 + Spreadsheet.mmPetalHightMin
  sketch-geometry (7):
    g0: Circle CenterX=0 CenterY=2e-15 CenterZ=0 NormalX=0 NormalY=0 NormalZ=1 AngleXU=0 Radius=39.844
    g1: Circle CenterX=0 CenterY=2e-15 CenterZ=0 NormalX=0 NormalY=0 NormalZ=1 AngleXU=0 Radius=26.62
    g2: ArcOfCircle CenterX=0 CenterY=2e-15 CenterZ=0 NormalX=0 NormalY=0 NormalZ=1 AngleXU=0 Radius=20.4 StartAngle=3.89517 EndAngle=6.7757
    g3: LineSegment StartX=19.5933 StartY=5.67991 StartZ=0 EndX=23.46 EndY=5.67991 EndZ=0
    g4: LineSegment StartX=23.46 StartY=5.67991 StartZ=0 EndX=23.46 EndY=-5.67991 EndZ=0
    g5: LineSegment StartX=23.46 StartY=-5.67991 StartZ=0 EndX=19.5933 EndY=-5.67991 EndZ=0
    g6: ArcOfCircle CenterX=0 CenterY=2e-15 CenterZ=0 NormalX=0 NormalY=0 NormalZ=1 AngleXU=0 Radius=20.4 StartAngle=6.00103 EndAngle=6.56534
  constraints (17):
    c: Diameter(g1) = 53.24
    c: Diameter(g2) = 40.8
    c: Coincident(g3,g4)
    c: Coincident(g4,g5)
    c: Coincident(g0,g2)
    c: Vertical(g4)
    c: DistanceX(g-1,g4) = 23.46
    c: Coincident(g6,g0)
    c: Coincident(g6,g3)
    c: Coincident(g6,g5)
    c: Diameter(g6) = 40.8
    c: Symmetric(g3,g5,g-1)
    c: DistanceY(g5,g3) = 11.3598
    c: Horizontal(g5)
    c: Horizontal(g3)
    c: Coincident(g1,g6)
    c: Coincident(g-1,g6)
FEATURE [PartDesign::SubtractiveLoft] SubtractiveLoft  label="PetalBodySubtractiveLoft"
  BaseFeature = -> Pad012
  Closed = false
  Placement = pos=(0,0,0) rot=(0.57735,0.57735,0.57735;2.0944rad)
  Profile = -> Sketch031
  Ruled = false
  Sections = -> [Sketch032]
FEATURE [PartDesign::PolarPattern] PolarPattern  label="ExisFixatorBodyPolarPattern"
  Angle = 360
  Axis = -> Sketch027 [N_Axis]
  BaseFeature = -> SubtractiveLoft
  Occurrences = 3
  Originals = -> [Pad012,AdditiveLoft,SubtractiveLoft]
  Placement = pos=(0,0,0) rot=(0.57735,0.57735,0.57735;2.0944rad)
FEATURE [PartDesign::Chamfer] Chamfer001
  Angle = 45
  Base = -> PolarPattern [Edge38,Edge9,Edge5,Edge23,Edge65,Edge59,Edge69,Edge47,Edge41]
  BaseFeature = -> PolarPattern
  ChamferType = 1
  FlipDirection = false
  Placement = pos=(0,0,0) rot=(0.57735,0.57735,0.57735;2.0944rad)
  Size = 2
  Size2 = 1
  SupportTransform = false
  UseAllEdges = false
FEATURE [PartDesign::Body] Body007  label="AxisFixatorBody"
  Group = -> [Sketch027,Pad012,Sketch031,Sketch032,SubtractiveLoft,PolarPattern,Chamfer001]
  Origin = -> Origin013
  Tip = -> Chamfer001
COMPONENT P5 — recipe-attached ("PetalMountingTemplate", modeled in this document).
Construction recipe (the document's own serialized feature program — sketch geometry with constraints, then the solid features built on it; lengths are millimeters unless a unit is written):

FEATURE [Sketcher::SketchObject] Sketch035  label="CommonFixatorScatch001"
  AttachmentOffset = pos=(0,0,16.32) rot=(0,0,1;0rad)
  FullyConstrained = false
  MapMode = 5
  Placement = pos=(16.32,-3.6e-15,3.6e-15) rot=(0.57735,0.57735,0.57735;2.0944rad)
  Support = -> [YZ_Plane013]
  expr: .AttachmentOffset.Base.z = Spreadsheet.mmFixatorHight * 0.8
  expr: Constraints[0] = Spreadsheet.mmAxisTubeDia + 2 * Spreadsheet.mmFixatorThick
  expr: Constraints[24] = Spreadsheet.mmBaseWidth
  expr: Constraints[3] = Spreadsheet.mmAxisTubeDia
  sketch-geometry (9):
    g0: Circle CenterX=0 CenterY=0 CenterZ=0 NormalX=0 NormalY=0 NormalZ=1 AngleXU=0 Radius=26.62
    g1: LineSegment StartX=0 StartY=0 StartZ=0 EndX=49.303 EndY=28.4651 EndZ=0
    g2: ArcOfCircle CenterX=0 CenterY=0 CenterZ=0 NormalX=0 NormalY=0 NormalZ=1 AngleXU=0 Radius=20.4 StartAngle=4.71235 EndAngle=6.7955
    g3: LineSegment StartX=0 StartY=-20.4 StartZ=0 EndX=0 EndY=-39.1443 EndZ=0
    g4: LineSegment StartX=0 StartY=-39.1443 StartZ=0 EndX=6.1036 EndY=-42.6683 EndZ=0
    g5: LineSegment StartX=6.1036 StartY=-42.6683 StartZ=0 EndX=40.0036 EndY=16.0483 EndZ=0
    g6: LineSegment StartX=40.0036 StartY=16.0483 StartZ=0 EndX=33.9 EndY=19.5722 EndZ=0
    g7: LineSegment StartX=33.9 StartY=19.5722 StartZ=0 EndX=17.6669 EndY=10.2 EndZ=0
    g8: ArcOfCircle CenterX=0 CenterY=0 CenterZ=0 NormalX=0 NormalY=0 NormalZ=1 AngleXU=0 Radius=20.4 StartAngle=4.71239 EndAngle=6.80678
  constraints (25):
    c: Diameter(g0) = 53.24
    c: Angle(g-1,g1) = 0.523599
    c: PointOnObject(g6,g1)
    c: Diameter(g2) = 40.8
    c: Vertical(g3)
    c: Coincident(g3,g4)
    c: Coincident(g4,g5)
    c: Coincident(g5,g6)
    c: Coincident(g6,g7)
    c: PointOnObject(g3,g-2)
    c: Parallel(g4,g6)
    c: Perpendicular(g5,g4)
    c: Tangent(g0,g5)
    c: PointOnObject(g8,g1)
    c: Coincident(g8,g7)
    c: PointOnObject(g8,g-2)
    c: PointOnObject(g8,g-1)
    c: PointOnObject(g8,g2)
    c: Coincident(g3,g8)
    c: Equal(g4,g6)
    c: Equal(g7,g3)
    c: Coincident(g2,g1)
    c: Coincident(g8,g1)
    c: Coincident(g8,g0)
    c: Distance(g4,g5) = 67.8
FEATURE [PartDesign::Pad] Pad013  label="AxisFixatorBodyPad001"
  Direction = (1,-2e-16,3e-16)
  Length = 6.12
  Length2 = 10
  Placement = pos=(0,0,0) rot=(0.57735,0.57735,0.57735;2.0944rad)
  Profile = -> Sketch035
  ReferenceAxis = -> Sketch035 [N_Axis]
  Type = 0
  expr: Length = Spreadsheet.mmFixatorHight * 0.3
FEATURE [Sketcher::SketchObject] Sketch038  label="MaxPetalBase004"
  FullyConstrained = false
  MapMode = 5
  Placement = pos=(0,0,0) rot=(0.57735,0.57735,0.57735;2.0944rad)
  Support = -> [YZ_Plane013]
  expr: Constraints[0] = Spreadsheet.mmAxisTubeDia + 2 * Spreadsheet.mmFixatorThick
  expr: Constraints[10] = Spreadsheet.mmAxisTubeDia
  expr: Constraints[15] = Spreadsheet.mmPetalPocketWidth
  expr: Constraints[1] = Spreadsheet.mmAxisTubeDia
  expr: Constraints[6] = Spreadsheet.mmAxisTubeDia * 2
  sketch-geometry (7):
    g0: Circle CenterX=0 CenterY=2.5e-15 CenterZ=0 NormalX=0 NormalY=0 NormalZ=1 AngleXU=0 Radius=39.855
    g1: Circle CenterX=0 CenterY=-1.1e-15 CenterZ=0 NormalX=0 NormalY=0 NormalZ=1 AngleXU=0 Radius=26.62
    g2: ArcOfCircle CenterX=0 CenterY=2.5e-15 CenterZ=0 NormalX=0 NormalY=0 NormalZ=1 AngleXU=0 Radius=20.4 StartAngle=5.6709 EndAngle=6.80795
    g3: LineSegment StartX=19.5933 StartY=5.67991 StartZ=0 EndX=81.6 EndY=5.67991 EndZ=0
    g4: LineSegment StartX=81.6 StartY=5.67991 StartZ=0 EndX=81.6 EndY=-5.67991 EndZ=0
    g5: LineSegment StartX=81.6 StartY=-5.67991 StartZ=0 EndX=19.5933 EndY=-5.67991 EndZ=0
    g6: ArcOfCircle CenterX=0 CenterY=2.5e-15 CenterZ=0 NormalX=0 NormalY=0 NormalZ=1 AngleXU=0 Radius=20.4 StartAngle=6.00103 EndAngle=6.56534
  constraints (16):
    c: Diameter(g1) = 53.24
    c: Diameter(g2) = 40.8
    c: Coincident(g3,g4)
    c: Coincident(g4,g5)
    c: Coincident(g0,g2)
    c: Vertical(g4)
    c: DistanceX(g-1,g4) = 81.6
    c: Coincident(g6,g0)
    c: Coincident(g6,g3)
    c: Coincident(g6,g5)
    c: Diameter(g6) = 40.8
    c: Horizontal(g3)
    c: Horizontal(g5)
    c: PointOnObject(g6,g-2)
    c: Symmetric(g3,g5,g-1)
    c: DistanceY(g5,g3) = 11.3598
FEATURE [Sketcher::SketchObject] Sketch039  label="MinPetalBase003"
  AttachmentOffset = pos=(0,0,20.4) rot=(0,0,1;0rad)
  FullyConstrained = false
  MapMode = 5
  Placement = pos=(20.4,-4.5e-15,4.5e-15) rot=(0.57735,0.57735,0.57735;2.0944rad)
  Support = -> [YZ_Plane013]
  expr: .AttachmentOffset.Base.z = Spreadsheet.mmFixatorHight
  expr: Constraints[0] = Spreadsheet.mmAxisTubeDia + 2 * Spreadsheet.mmFixatorThick
  expr: Constraints[10] = Spreadsheet.mmAxisTubeDia
  expr: Constraints[11] = Spreadsheet.mmPetalPocketWidth
  expr: Constraints[1] = Spreadsheet.mmAxisTubeDia
  expr: Constraints[6] = Spreadsheet.mmAxisTubeDia * 2
  sketch-geometry (7):
    g0: Circle CenterX=0 CenterY=2.1e-15 CenterZ=0 NormalX=0 NormalY=0 NormalZ=1 AngleXU=0 Radius=39.844
    g1: Circle CenterX=0 CenterY=2.1e-15 CenterZ=0 NormalX=0 NormalY=0 NormalZ=1 AngleXU=0 Radius=26.62
    g2: ArcOfCircle CenterX=0 CenterY=2.1e-15 CenterZ=0 NormalX=0 NormalY=0 NormalZ=1 AngleXU=0 Radius=20.4 StartAngle=3.90517 EndAngle=6.76925
    g3: LineSegment StartX=19.5933 StartY=5.67991 StartZ=0 EndX=81.6 EndY=5.67991 EndZ=0
    g4: LineSegment StartX=81.6 StartY=5.67991 StartZ=0 EndX=81.6 EndY=-5.67991 EndZ=0
    g5: LineSegment StartX=81.6 StartY=-5.67991 StartZ=0 EndX=19.5933 EndY=-5.67991 EndZ=0
    g6: ArcOfCircle CenterX=0 CenterY=2.1e-15 CenterZ=0 NormalX=0 NormalY=0 NormalZ=1 AngleXU=0 Radius=20.4 StartAngle=6.00103 EndAngle=6.56534
  constraints (17):
    c: Diameter(g1) = 53.24
    c: Diameter(g2) = 40.8
    c: Coincident(g3,g4)
    c: Coincident(g4,g5)
    c: Coincident(g0,g2)
    c: Vertical(g4)
    c: DistanceX(g-1,g4) = 81.6
    c: Coincident(g6,g0)
    c: Coincident(g6,g3)
    c: Coincident(g6,g5)
    c: Diameter(g6) = 40.8
    c: DistanceY(g5,g3) = 11.3598
    c: Symmetric(g3,g5,g-1)
    c: Coincident(g1,g6)
    c: Coincident(g-1,g6)
    c: Horizontal(g3)
    c: Horizontal(g5)
FEATURE [PartDesign::SubtractiveLoft] SubtractiveLoft001  label="PetalBodySubtractiveLoft001"
  BaseFeature = -> Pad013
  Closed = false
  Placement = pos=(0,0,0) rot=(0.57735,0.57735,0.57735;2.0944rad)
  Profile = -> Sketch038
  Ruled = false
  Sections = -> [Sketch039]
FEATURE [PartDesign::PolarPattern] PolarPattern001  label="ExisFixatorBodyPolarPattern001"
  Angle = 360
  Axis = -> Sketch035 [N_Axis]
  BaseFeature = -> SubtractiveLoft001
  Occurrences = 3
  Originals = -> [Pad013,SubtractiveLoft001]
  Placement = pos=(0,0,0) rot=(0.57735,0.57735,0.57735;2.0944rad)
FEATURE [Sketcher::SketchObject] Sketch040  label="CommonFixatorScatch002"
  AttachmentOffset = pos=(0,0,16.32) rot=(0,0,1;0rad)
  FullyConstrained = true
  MapMode = 5
  Placement = pos=(16.32,-3.6e-15,3.6e-15) rot=(0.57735,0.57735,0.57735;2.0944rad)
  Support = -> [YZ_Plane013]
  expr: .AttachmentOffset.Base.z = Spreadsheet.mmFixatorHight * 0.8
  expr: Constraints[11] = Spreadsheet.mmAxisTubeDia * 2
  expr: Constraints[14] = Spreadsheet.mmTemplatePartsConnectorDia - 2 * Spreadsheet.mmAirSpace
  expr: Constraints[15] = Spreadsheet.mmTemplatePartsConnectorDia * 3 / 2
  expr: Constraints[1] = Spreadsheet.mmAxisTubeDia + 2 * Spreadsheet.mmFixatorThick
  expr: Constraints[27] = Spreadsheet.mmAirSpace
  expr: Constraints[33] = Spreadsheet.mmTemplatePartsConnectorDia / 3
  expr: Constraints[41] = Spreadsheet.mmTemplatePartsConnectorDia
  expr: Constraints[43] = Spreadsheet.mmTemplatePartsConnectorDia * 2 / 3
  expr: Constraints[45] = Spreadsheet.mmTemplatePartsConnectorDia * 2 / 3 - 2 * Spreadsheet.mmAirSpace
  expr: Constraints[52] = Spreadsheet.mmTemplatePartsConnectorDia / 3
  expr: Constraints[55] = Spreadsheet.mmTemplatePartsConnectorDia / 2
  sketch-geometry (19):
    g0: Circle CenterX=0 CenterY=0 CenterZ=0 NormalX=0 NormalY=0 NormalZ=1 AngleXU=0 Radius=40.8
    g1: Circle CenterX=0 CenterY=0 CenterZ=0 NormalX=0 NormalY=0 NormalZ=1 AngleXU=0 Radius=26.62
    g2: LineSegment StartX=-35.5321 StartY=20.0526 StartZ=0 EndX=-28.3499 EndY=15.9059 EndZ=0
    g3: LineSegment StartX=22.767 StartY=-13.6064 StartZ=0 EndX=23.167 EndY=-12.9136 EndZ=0
    g4: LineSegment StartX=23.167 StartY=-12.9136 StartZ=0 EndX=21.4554 EndY=-11.9254 EndZ=0
    g5: LineSegment StartX=-35.1321 StartY=20.7454 StartZ=0 EndX=-35.5321 EndY=20.0526 EndZ=0
    g6: LineSegment StartX=23.0536 StartY=-13.31 StartZ=0 EndX=-35.3338 EndY=20.4 EndZ=0
    g7: ArcOfCircle CenterX=-26.42 CenterY=17.1754 CenterZ=0 NormalX=0 NormalY=0 NormalZ=1 AngleXU=0 Radius=2.31 StartAngle=4.65418 EndAngle=10.0066
    g8: LineSegment StartX=-26.5543 StartY=14.8693 StartZ=0 EndX=18.3629 EndY=-11.0637 EndZ=0
    g9: LineSegment StartX=-29.5129 StartY=17.5011 StartZ=0 EndX=-35.1321 EndY=20.7454 EndZ=0
    g10: LineSegment StartX=-35.1321 StartY=20.7454 StartZ=0 EndX=-35.5321 EndY=20.0526 EndZ=0
    g11: LineSegment StartX=-35.5321 StartY=20.0526 StartZ=0 EndX=22.851 EndY=-13.6549 EndZ=0
    g12: LineSegment StartX=22.851 StartY=-13.6549 StartZ=0 EndX=23.251 EndY=-12.9621 EndZ=0
    g13: LineSegment StartX=23.251 StartY=-12.9621 StartZ=0 EndX=-35.1321 EndY=20.7454 EndZ=0
    g14: ArcOfCircle CenterX=-26.42 CenterY=17.1754 CenterZ=0 NormalX=0 NormalY=0 NormalZ=1 AngleXU=0 Radius=3.11 StartAngle=5.34093 EndAngle=9.31984
    g15: ArcOfCircle CenterX=20.188 CenterY=-12.0474 CenterZ=0 NormalX=0 NormalY=0 NormalZ=1 AngleXU=0 Radius=2.07333 StartAngle=2.64723 EndAngle=5.73035
    g16: ArcOfCircle CenterX=20.188 CenterY=-12.0474 CenterZ=0 NormalX=0 NormalY=0 NormalZ=1 AngleXU=0 Radius=1.27333 StartAngle=1.99844 EndAngle=6.37914
    g17: LineSegment StartX=21.9524 StartY=-13.1361 StartZ=0 EndX=22.767 EndY=-13.6064 EndZ=0
    g18: LineSegment StartX=19.6599 StartY=-10.8888 StartZ=0 EndX=-24.5914 EndY=14.6597 EndZ=0
  constraints (56):
    c: PointOnObject(g6,g0)
    c: Diameter(g1) = 53.24
    c: Coincident(g0,g1)
    c: Coincident(g0,g-1)
    c: Coincident(g3,g4)
    c: Coincident(g9,g5)
    c: Coincident(g5,g2)
    c: Perpendicular(g3,g2)
    c: Symmetric(g2,g9,g6)
    c: Symmetric(g17,g3,g6)
    c: PointOnObject(g0,g6)
    c: Diameter(g0) = 81.6
    c: PointOnObject(g6,g1)
    c: Angle(g-1,g6) = 2.61799
    c: Diameter(g7) = 4.62
    c: Distance(g7,g5) = 9.33
    c: Parallel(g9,g4)
    c: Parallel(g2,g8)
    c: Coincident(g10,g11)
    c: Coincident(g11,g12)
    c: Coincident(g12,g13)
    c: Coincident(g13,g10)
    c: PointOnObject(g10,g0)
    c: Symmetric(g10,g10,g6)
    c: Parallel(g6,g13)
    c: Parallel(g11,g13)
    c: Coincident(g5,g10)
    c: Distance(g3,g3) = 0.8
    c: Coincident(g3,g17)
    c: PointOnObject(g11,g1)
    c: PointOnObject(g12,g1)
    c: PointOnObject(g3,g13)
    c: Distance(g6,g3) = 0.1
    c: Distance(g2,g8) = 2.07333
    c: PointOnObject(g14,g13)
    c: PointOnObject(g14,g13)
    c: PointOnObject(g18,g14)
    c: PointOnObject(g9,g14)
    c: Coincident(g7,g8)
    c: Coincident(g7,g2)
    c: Coincident(g14,g7)
    c: Diameter(g14) = 6.22
    c: PointOnObject(g18,g13)
    c: Diameter(g15) = 4.14667
    c: Coincident(g15,g16)
    c: Diameter(g16) = 2.54667
    c: Coincident(g15,g8)
    c: PointOnObject(g8,g11)
    c: Coincident(g17,g15)
    c: PointOnObject(g15,g11)
    c: Coincident(g4,g16)
    c: Coincident(g18,g16)
    c: Distance(g16,g4) = 2.07333
    c: PointOnObject(g4,g13)
    c: PointOnObject(g16,g13)
    c: Distance(g15,g12) = 3.11
FEATURE [PartDesign::Pocket] Pocket003
  BaseFeature = -> PolarPattern001
  Direction = (-1,2e-16,-3e-16)
  Length = 40.8
  Length2 = 5
  Midplane = true
  Placement = pos=(0,0,0) rot=(0.57735,0.57735,0.57735;2.0944rad)
  Profile = -> Sketch040
  ReferenceAxis = -> Sketch040 [N_Axis]
  Type = 0
  expr: Length = Spreadsheet.mmAxisTubeDia
FEATURE [PartDesign::Chamfer] Chamfer002
  Angle = 45
  Base = -> Pocket003 [Edge1,Edge35,Edge31,Edge98,Edge94,Edge47,Edge12]
  BaseFeature = -> Pocket003
  ChamferType = 0
  FlipDirection = false
  Placement = pos=(0,0,0) rot=(0.57735,0.57735,0.57735;2.0944rad)
  Size = 1
  Size2 = 1
  SupportTransform = false
  UseAllEdges = false
FEATURE [PartDesign::Chamfer] Chamfer003
  Angle = 45
  Base = -> Chamfer002 [Edge56,Edge17,Edge3,Edge28]
  BaseFeature = -> Chamfer002
  ChamferType = 0
  FlipDirection = false
  Placement = pos=(0,0,0) rot=(0.57735,0.57735,0.57735;2.0944rad)
  Size = 1
  Size2 = 1
  SupportTransform = false
  UseAllEdges = false
FEATURE [PartDesign::Chamfer] Chamfer004
  Angle = 45
  Base = -> Chamfer003 [Edge56,Edge61,Edge130,Edge128,Edge73,Edge75]
  BaseFeature = -> Chamfer003
  ChamferType = 0
  FlipDirection = false
  Placement = pos=(0,0,0) rot=(0.57735,0.57735,0.57735;2.0944rad)
  Size = 1
  Size2 = 1
  SupportTransform = false
  UseAllEdges = false
FEATURE [PartDesign::Fillet] Fillet
  Base = -> Chamfer004 [Edge66,Edge26]
  BaseFeature = -> Chamfer004
  Placement = pos=(0,0,0) rot=(0.57735,0.57735,0.57735;2.0944rad)
  Radius = 1
  SupportTransform = false
  UseAllEdges = false
FEATURE [PartDesign::Body] Body010  label="AxisFixatorTemplate"
  Group = -> [Sketch035,Pad013,Sketch038,Sketch039,SubtractiveLoft001,PolarPattern001,Sketch040,Pocket003,Chamfer002,Chamfer003,Chamfer004,Fillet]
  Origin = -> Origin019
  Tip = -> Fillet
COMPONENT P6 — recipe-attached ("AxisFixatorAbsolete", modeled in this document).
Construction recipe (the document's own serialized feature program — sketch geometry with constraints, then the solid features built on it; lengths are millimeters unless a unit is written):

FEATURE [Sketcher::SketchObject] Sketch041  label="CommonFixatorScatch003"
  FullyConstrained = false
  MapMode = 5
  Placement = pos=(0,0,0) rot=(0.57735,0.57735,0.57735;2.0944rad)
  Support = -> [YZ_Plane013]
  expr: Constraints[22] = 2 * (Spreadsheet.mmAxisTubeDia / 2 + Spreadsheet.mmFixatorThick) / cos(Spreadsheet.angPetal / 2)
  expr: Constraints[23] = Spreadsheet.mmHingeHight
  expr: Constraints[31] = Spreadsheet.mmAxisTubeDia
  expr: Constraints[64] = Spreadsheet.mmPetalWidth + Spreadsheet.mmAirSpace
  expr: Constraints[67] = Spreadsheet.mmAxisTubeDia / 2 + Spreadsheet.mmPetalHightMax + Spreadsheet.mmTwoSideTapeThick + Spreadsheet.mmAirSpace
  sketch-geometry (24):
    g0: LineSegment StartX=33.9 StartY=19.5722 StartZ=0 EndX=-33.9 EndY=19.5722 EndZ=0
    g1: LineSegment StartX=-33.9 StartY=19.5722 StartZ=0 EndX=0 EndY=-39.1443 EndZ=0
    g2: LineSegment StartX=0 StartY=-39.1443 StartZ=0 EndX=33.9 EndY=19.5722 EndZ=0
    g3: Circle CenterX=0 CenterY=0 CenterZ=0 NormalX=0 NormalY=0 NormalZ=1 AngleXU=0 Radius=39.1443
    g4: LineSegment StartX=-23.8668 StartY=13.7795 StartZ=0 EndX=-23.8668 EndY=-13.7795 EndZ=0
    g5: LineSegment StartX=-23.8668 StartY=-13.7795 StartZ=0 EndX=0 EndY=-27.5591 EndZ=0
    g6: LineSegment StartX=0 StartY=-27.5591 StartZ=0 EndX=23.8668 EndY=-13.7795 EndZ=0
    g7: LineSegment StartX=23.8668 StartY=-13.7795 StartZ=0 EndX=23.8668 EndY=13.7795 EndZ=0
    g8: LineSegment StartX=23.8668 StartY=13.7795 StartZ=0 EndX=0 EndY=27.5591 EndZ=0
    g9: LineSegment StartX=-1e-16 StartY=27.5591 StartZ=0 EndX=-23.8668 EndY=13.7795 EndZ=0
    g10: Circle CenterX=0 CenterY=0 CenterZ=0 NormalX=0 NormalY=0 NormalZ=1 AngleXU=0 Radius=27.5591
    g11: LineSegment StartX=0 StartY=0 StartZ=0 EndX=33.9 EndY=19.5722 EndZ=0
    g12: ArcOfCircle CenterX=0 CenterY=0 CenterZ=0 NormalX=0 NormalY=0 NormalZ=1 AngleXU=0 Radius=20.4 StartAngle=4.5996 EndAngle=6.79538
    g13: LineSegment StartX=0 StartY=-20.4 StartZ=0 EndX=0 EndY=-39.1443 EndZ=0
    g14: LineSegment StartX=0 StartY=-39.1443 StartZ=0 EndX=6.91684 EndY=-43.1378 EndZ=0
    g15: LineSegment StartX=6.91684 StartY=-43.1378 StartZ=0 EndX=40.8168 EndY=15.5787 EndZ=0
    g16: LineSegment StartX=40.8168 StartY=15.5787 StartZ=0 EndX=33.9 EndY=19.5722 EndZ=0
    g17: LineSegment StartX=33.9 StartY=19.5722 StartZ=0 EndX=17.6669 EndY=10.2 EndZ=0
    g18: LineSegment StartX=14.7156 StartY=-14.1284 StartZ=0 EndX=18.6289 EndY=-20.9065 EndZ=0
    g19: LineSegment StartX=18.6289 StartY=-20.9065 StartZ=0 EndX=8.79105 EndY=-26.5864 EndZ=0
    g20: LineSegment StartX=8.79105 StartY=-26.5864 StartZ=0 EndX=4.87772 EndY=-19.8083 EndZ=0
    g21: ArcOfCircle CenterX=0 CenterY=0 CenterZ=0 NormalX=0 NormalY=0 NormalZ=1 AngleXU=0 Radius=20.4 StartAngle=4.71239 EndAngle=4.95383
    g22: ArcOfCircle CenterX=0 CenterY=0 CenterZ=0 NormalX=0 NormalY=0 NormalZ=1 AngleXU=0 Radius=20.4 StartAngle=5.51814 EndAngle=6.80678
    g23: LineSegment StartX=0 StartY=0 StartZ=0 EndX=19.5722 EndY=-33.9 EndZ=0
  constraints (64):
    c: Coincident(g0,g1)
    c: Coincident(g1,g2)
    c: Coincident(g2,g0)
    c: Equal(g0,g1)
    c: Equal(g0,g2)
    c: PointOnObject(g0,g3)
    c: Coincident(g4,g5)
    c: Coincident(g5,g6)
    c: Coincident(g6,g7)
    c: Coincident(g7,g8)
    c: Coincident(g8,g9)
    c: Coincident(g9,g4)
    c: Equal(g4, g5-g9) x5
    c: PointOnObject(g4,g10)
    c: PointOnObject(g5,g10)
    c: PointOnObject(g6,g10)
    c: PointOnObject(g7,g10)
    c: PointOnObject(g8,g10)
    c: Diameter(g10) = 55.1181
    c: Distance(g2) = 67.8
    c: PointOnObject(g5,g-2)
    c: PointOnObject(g4,g10)
    c: Angle(g-1,g11) = 0.523599
    c: Coincident(g3,g10)
    c: Coincident(g3,g11)
    c: Coincident(g3,g-1)
    c: PointOnObject(g0,g11)
    c: Diameter(g12) = 40.8
    c: Coincident(g12,g3)
    c: Vertical(g13)
    c: Coincident(g13,g14)
    c: Coincident(g14,g15)
    c: Coincident(g15,g16)
    c: Coincident(g16,g17)
    c: Coincident(g19,g20)
    c: Coincident(g1,g13)
    c: Coincident(g0,g16)
    c: Equal(g12,g21)
    c: Coincident(g12,g21)
    c: PointOnObject(g13,g-2)
    c: PointOnObject(g13,g3)
    c: Parallel(g2,g15)
    c: Parallel(g14,g16)
    c: Perpendicular(g15,g14)
    c: Tangent(g10,g15)
    c: PointOnObject(g11,g3)
    c: Coincident(g21,g22)
    c: PointOnObject(g17,g11)
    c: Coincident(g20,g21)
    c: Coincident(g21,g13)
    c: Coincident(g22,g18)
    c: PointOnObject(g22,g11)
    c: Coincident(g22,g17)
    c: PointOnObject(g17,g11)
    c: Perpendicular(g20,g19)
    c: Perpendicular(g19,g18)
    c: Coincident(g23,g21)
    c: Angle(g23,g-2) = 2.61799
    c: PointOnObject(g23,g3)
    c: Symmetric(g20,g18,g23)
    c: Distance(g20,g18) = 11.3598
    c: Perpendicular(g23,g19)
    c: Coincident(g18,g19)
    c: Distance(g21,g19) = 27.42
FEATURE [PartDesign::Pad] Pad014  label="AxisFixatorBodyPad002"
  Direction = (1,-2e-16,3e-16)
  Length = 20.4
  Length2 = 10
  Placement = pos=(0,0,0) rot=(0.57735,0.57735,0.57735;2.0944rad)
  Profile = -> Sketch041
  ReferenceAxis = -> Sketch041 [N_Axis]
  Type = 0
  expr: Length = Spreadsheet.mmFixatorHight
FEATURE [Sketcher::SketchObject] Sketch044  label="MaxPetalBase006"
  FullyConstrained = false
  MapMode = 5
  Placement = pos=(0,0,0) rot=(0.57735,0.57735,0.57735;2.0944rad)
  Support = -> [YZ_Plane013]
  expr: Constraints[0] = Spreadsheet.mmAxisTubeDia + 2 * Spreadsheet.mmFixatorThick
  expr: Constraints[14] = Spreadsheet.mmPetalWidth + Spreadsheet.mmAirSpace
  expr: Constraints[1] = Spreadsheet.mmAxisTubeDia
  expr: Constraints[5] = Spreadsheet.mmAxisTubeDia / 2 + Spreadsheet.mmPetalHightMax
  expr: Constraints[9] = Spreadsheet.mmAxisTubeDia
  sketch-geometry (7):
    g0: Circle CenterX=0 CenterY=0 CenterZ=0 NormalX=0 NormalY=0 NormalZ=1 AngleXU=0 Radius=39.855
    g1: Circle CenterX=0 CenterY=0 CenterZ=0 NormalX=0 NormalY=0 NormalZ=1 AngleXU=0 Radius=26.62
    g2: ArcOfCircle CenterX=0 CenterY=0 CenterZ=0 NormalX=0 NormalY=0 NormalZ=1 AngleXU=0 Radius=20.4 StartAngle=5.86249 EndAngle=6.74499
    g3: LineSegment StartX=19.5933 StartY=5.67991 StartZ=0 EndX=26.52 EndY=5.67991 EndZ=0
    g4: LineSegment StartX=26.52 StartY=5.67991 StartZ=0 EndX=26.52 EndY=-5.67991 EndZ=0
    g5: LineSegment StartX=26.52 StartY=-5.67991 StartZ=0 EndX=19.5933 EndY=-5.67991 EndZ=0
    g6: ArcOfCircle CenterX=0 CenterY=0 CenterZ=0 NormalX=0 NormalY=0 NormalZ=1 AngleXU=0 Radius=20.4 StartAngle=6.00103 EndAngle=6.56534
  constraints (22):
    c: Diameter(g1) = 53.24
    c: Diameter(g2) = 40.8
    c: Coincident(g3,g4)
    c: Coincident(g4,g5)
    c: Coincident(g0,g2)
    c: DistanceX(g-1,g4) = 26.52
    c: Coincident(g6,g0)
    c: Coincident(g6,g3)
    c: Coincident(g6,g5)
    c: Diameter(g6) = 40.8
    c: Coincident(g6,g-1)
    c: Symmetric(g3,g5,g-1)
    c: Horizontal(g5)
    c: Horizontal(g3)
    c: DistanceY(g5,g3) = 11.3598
    c: Coincident(g6,g1)
    c: PointOnObject(g6,g-2)
    c: PointOnObject(g6,g-1)
    c: PointOnObject(g6,g5)
    c: PointOnObject(g6,g3)
    c: PointOnObject(g3,g6)
    c: Vertical(g4)
FEATURE [Sketcher::SketchObject] Sketch045  label="MinPetalBase005"
  AttachmentOffset = pos=(0,0,18.36) rot=(0,0,1;0rad)
  FullyConstrained = false
  MapMode = 5
  Placement = pos=(18.36,-4.1e-15,4.1e-15) rot=(0.57735,0.57735,0.57735;2.0944rad)
  Support = -> [YZ_Plane013]
  expr: .AttachmentOffset.Base.z = Spreadsheet.mmFixatorHight * 0.9
  expr: Constraints[0] = Spreadsheet.mmAxisTubeDia + 2 * Spreadsheet.mmFixatorThick
  expr: Constraints[10] = Spreadsheet.mmAxisTubeDia
  expr: Constraints[12] = Spreadsheet.mmPetalWidth + Spreadsheet.mmAirSpace
  expr: Constraints[1] = Spreadsheet.mmAxisTubeDia
  expr: Constraints[6] = Spreadsheet.mmAxisTubeDia / 2 + Spreadsheet.mmPetalHightMin
  sketch-geometry (7):
    g0: Circle CenterX=0 CenterY=2.3e-15 CenterZ=0 NormalX=0 NormalY=0 NormalZ=1 AngleXU=0 Radius=39.844
    g1: Circle CenterX=0 CenterY=2.3e-15 CenterZ=0 NormalX=0 NormalY=0 NormalZ=1 AngleXU=0 Radius=26.62
    g2: ArcOfCircle CenterX=0 CenterY=2.3e-15 CenterZ=0 NormalX=0 NormalY=0 NormalZ=1 AngleXU=0 Radius=20.4 StartAngle=3.8687 EndAngle=6.82101
    g3: LineSegment StartX=19.5933 StartY=5.67991 StartZ=0 EndX=23.46 EndY=5.67991 EndZ=0
    g4: LineSegment StartX=23.46 StartY=5.67991 StartZ=0 EndX=23.46 EndY=-5.67991 EndZ=0
    g5: LineSegment StartX=23.46 StartY=-5.67991 StartZ=0 EndX=19.5933 EndY=-5.67991 EndZ=0
    g6: ArcOfCircle CenterX=0 CenterY=2.3e-15 CenterZ=0 NormalX=0 NormalY=0 NormalZ=1 AngleXU=0 Radius=20.4 StartAngle=6.00103 EndAngle=6.56534
  constraints (17):
    c: Diameter(g1) = 53.24
    c: Diameter(g2) = 40.8
    c: Coincident(g3,g4)
    c: Coincident(g4,g5)
    c: Coincident(g0,g2)
    c: Vertical(g4)
    c: DistanceX(g-1,g4) = 23.46
    c: Coincident(g6,g0)
    c: Coincident(g6,g3)
    c: Coincident(g6,g5)
    c: Diameter(g6) = 40.8
    c: Symmetric(g3,g5,g-1)
    c: DistanceY(g5,g3) = 11.3598
    c: Horizontal(g3)
    c: Horizontal(g5)
    c: Coincident(g6,g1)
    c: Coincident(g6,g-1)
FEATURE [PartDesign::SubtractiveLoft] SubtractiveLoft002  label="PetalBodySubtractiveLoft002"
  BaseFeature = -> Pad014
  Closed = false
  Placement = pos=(0,0,0) rot=(0.57735,0.57735,0.57735;2.0944rad)
  Profile = -> Sketch044
  Ruled = false
  Sections = -> [Sketch045]
FEATURE [PartDesign::PolarPattern] PolarPattern002  label="ExisFixatorBodyPolarPattern002"
  Angle = 360
  Axis = -> Sketch041 [N_Axis]
  BaseFeature = -> SubtractiveLoft002
  Occurrences = 3
  Originals = -> [Pad014,SubtractiveLoft002]
  Placement = pos=(0,0,0) rot=(0.57735,0.57735,0.57735;2.0944rad)
FEATURE [PartDesign::Body] Body011  label="AxisFixatorBody001"
  Group = -> [Sketch041,Pad014,Sketch044,Sketch045,SubtractiveLoft002,PolarPattern002]
  Origin = -> Origin021
  Tip = -> PolarPattern002
COMPONENT P7 — recipe-attached ("PetalPart", modeled in this document).
Construction recipe (the document's own serialized feature program — sketch geometry with constraints, then the solid features built on it; lengths are millimeters unless a unit is written):

FEATURE [Sketcher::SketchObject] Sketch029  label="MaxPetalBase"
  FullyConstrained = false
  MapMode = 5
  Placement = pos=(0,0,0) rot=(0.57735,0.57735,0.57735;2.0944rad)
  Support = -> [YZ_Plane015]
  expr: Constraints[0] = Spreadsheet.mmAxisTubeDia + 2 * Spreadsheet.mmFixatorThick
  expr: Constraints[12] = Spreadsheet.mmAxisTubeDia / 2 + Spreadsheet.mmPetalHightMax
  expr: Constraints[16] = Spreadsheet.mmPetalWidth
  expr: Constraints[1] = Spreadsheet.mmAxisTubeDia
  expr: Constraints[6] = Spreadsheet.mmAxisTubeDia + Spreadsheet.mmTwoSideTapeThick * 2
  sketch-geometry (7):
    g0: Circle CenterX=0 CenterY=0 CenterZ=0 NormalX=0 NormalY=0 NormalZ=1 AngleXU=0 Radius=39.8652
    g1: Circle CenterX=0 CenterY=0 CenterZ=0 NormalX=0 NormalY=0 NormalZ=1 AngleXU=0 Radius=26.62
    g2: ArcOfCircle CenterX=0 CenterY=0 CenterZ=0 NormalX=0 NormalY=0 NormalZ=1 AngleXU=0 Radius=20.4 StartAngle=3.89684 EndAngle=6.80091
    g3: LineSegment StartX=19.8084 StartY=5.27991 StartZ=0 EndX=26.52 EndY=5.27991 EndZ=0
    g4: LineSegment StartX=26.52 StartY=5.27991 StartZ=0 EndX=26.52 EndY=-5.27991 EndZ=0
    g5: LineSegment StartX=26.52 StartY=-5.27991 StartZ=0 EndX=19.8084 EndY=-5.27991 EndZ=0
    g6: ArcOfCircle CenterX=0 CenterY=0 CenterZ=0 NormalX=0 NormalY=0 NormalZ=1 AngleXU=0 Radius=20.5 StartAngle=6.02269 EndAngle=6.54368
  constraints (20):
    c: Diameter(g1) = 53.24
    c: Diameter(g2) = 40.8
    c: Coincident(g3,g4)
    c: Coincident(g4,g5)
    c: PointOnObject(g3,g2)
    c: Coincident(g6,g0)
    c: Diameter(g6) = 41
    c: Coincident(g1,g6)
    c: Coincident(g0,g2)
    c: Vertical(g4)
    c: PointOnObject(g3,g6)
    c: PointOnObject(g5,g6)
    c: DistanceX(g-1,g4) = 26.52
    c: Horizontal(g3)
    c: Horizontal(g5)
    c: Symmetric(g5,g3,g-1)
    c: DistanceY(g5,g3) = 10.5598
    c: Coincident(g-1,g6)
    c: PointOnObject(g6,g5)
    c: PointOnObject(g6,g3)
FEATURE [Sketcher::SketchObject] Sketch030  label="MinPetalBase"
  AttachmentOffset = pos=(0,0,20.4) rot=(0,0,1;0rad)
  FullyConstrained = false
  MapMode = 5
  Placement = pos=(20.4,-4.5e-15,4.5e-15) rot=(0.57735,0.57735,0.57735;2.0944rad)
  Support = -> [YZ_Plane015]
  expr: .AttachmentOffset.Base.z = Spreadsheet.mmFixatorHight
  expr: Constraints[0] = Spreadsheet.mmAxisTubeDia + 2 * Spreadsheet.mmFixatorThick
  expr: Constraints[11] = Spreadsheet.mmAxisTubeDia / 2 + Spreadsheet.mmPetalHightMin
  expr: Constraints[15] = Spreadsheet.mmPetalWidth
  expr: Constraints[1] = Spreadsheet.mmAxisTubeDia
  expr: Constraints[5] = Spreadsheet.mmAxisTubeDia + Spreadsheet.mmTwoSideTapeThick * 2
  sketch-geometry (7):
    g0: Circle CenterX=0 CenterY=1.8e-15 CenterZ=0 NormalX=0 NormalY=0 NormalZ=1 AngleXU=0 Radius=39.865
    g1: Circle CenterX=0 CenterY=1.8e-15 CenterZ=0 NormalX=0 NormalY=0 NormalZ=1 AngleXU=0 Radius=26.62
    g2: ArcOfCircle CenterX=0 CenterY=1.8e-15 CenterZ=0 NormalX=0 NormalY=0 NormalZ=1 AngleXU=0 Radius=20.4 StartAngle=3.86544 EndAngle=6.7404
    g3: LineSegment StartX=19.8084 StartY=5.27991 StartZ=0 EndX=23.46 EndY=5.27991 EndZ=0
    g4: LineSegment StartX=23.46 StartY=5.27991 StartZ=0 EndX=23.46 EndY=-5.27991 EndZ=0
    g5: LineSegment StartX=23.46 StartY=-5.27991 StartZ=0 EndX=19.8084 EndY=-5.27991 EndZ=0
    g6: ArcOfCircle CenterX=0 CenterY=1.8e-15 CenterZ=0 NormalX=0 NormalY=0 NormalZ=1 AngleXU=0 Radius=20.5 StartAngle=6.02269 EndAngle=6.54368
  constraints (20):
    c: Diameter(g1) = 53.24
    c: Diameter(g2) = 40.8
    c: Coincident(g3,g4)
    c: Coincident(g4,g5)
    c: Coincident(g6,g0)
    c: Diameter(g6) = 41
    c: Coincident(g1,g6)
    c: Coincident(g0,g2)
    c: Vertical(g4)
    c: PointOnObject(g3,g6)
    c: PointOnObject(g5,g6)
    c: DistanceX(g-1,g4) = 23.46
    c: PointOnObject(g6,g5)
    c: PointOnObject(g6,g3)
    c: Coincident(g6,g-1)
    c: DistanceY(g5,g3) = 10.5598
    c: Symmetric(g5,g3,g-1)
    c: Horizontal(g3)
    c: Horizontal(g5)
    c: PointOnObject(g6,g-2)
FEATURE [PartDesign::AdditiveLoft] AdditiveLoft  label="PetalBodyBodyAdditiveLoft"
  Closed = false
  Placement = pos=(0,0,0) rot=(0.57735,0.57735,0.57735;2.0944rad)
  Profile = -> Sketch029
  Ruled = false
  Sections = -> [Sketch030]
FEATURE [PartDesign::Chamfer] Chamfer
  Angle = 45
  Base = -> AdditiveLoft [Edge8,Edge9,Edge6,Edge3,Edge2,Edge1,Edge11,Edge5]
  BaseFeature = -> AdditiveLoft
  ChamferType = 0
  FlipDirection = false
  Placement = pos=(0,0,0) rot=(0.57735,0.57735,0.57735;2.0944rad)
  Size = 1
  Size2 = 1
  SupportTransform = false
  UseAllEdges = false
FEATURE [PartDesign::Body] Body008  label="PetalBodyPart"
  Group = -> [Sketch029,Sketch030,AdditiveLoft,Chamfer]
  Origin = -> Origin015
  Tip = -> Chamfer
PROVENANCE & LICENSES
A FreeCAD (.FCStd) document from a public repository crawl; recipes are the document's own serialized feature recipes (and, for linked parts, companion documents' recipes).
License: as declared in the source repository (recorded in the dataset sidecar).
